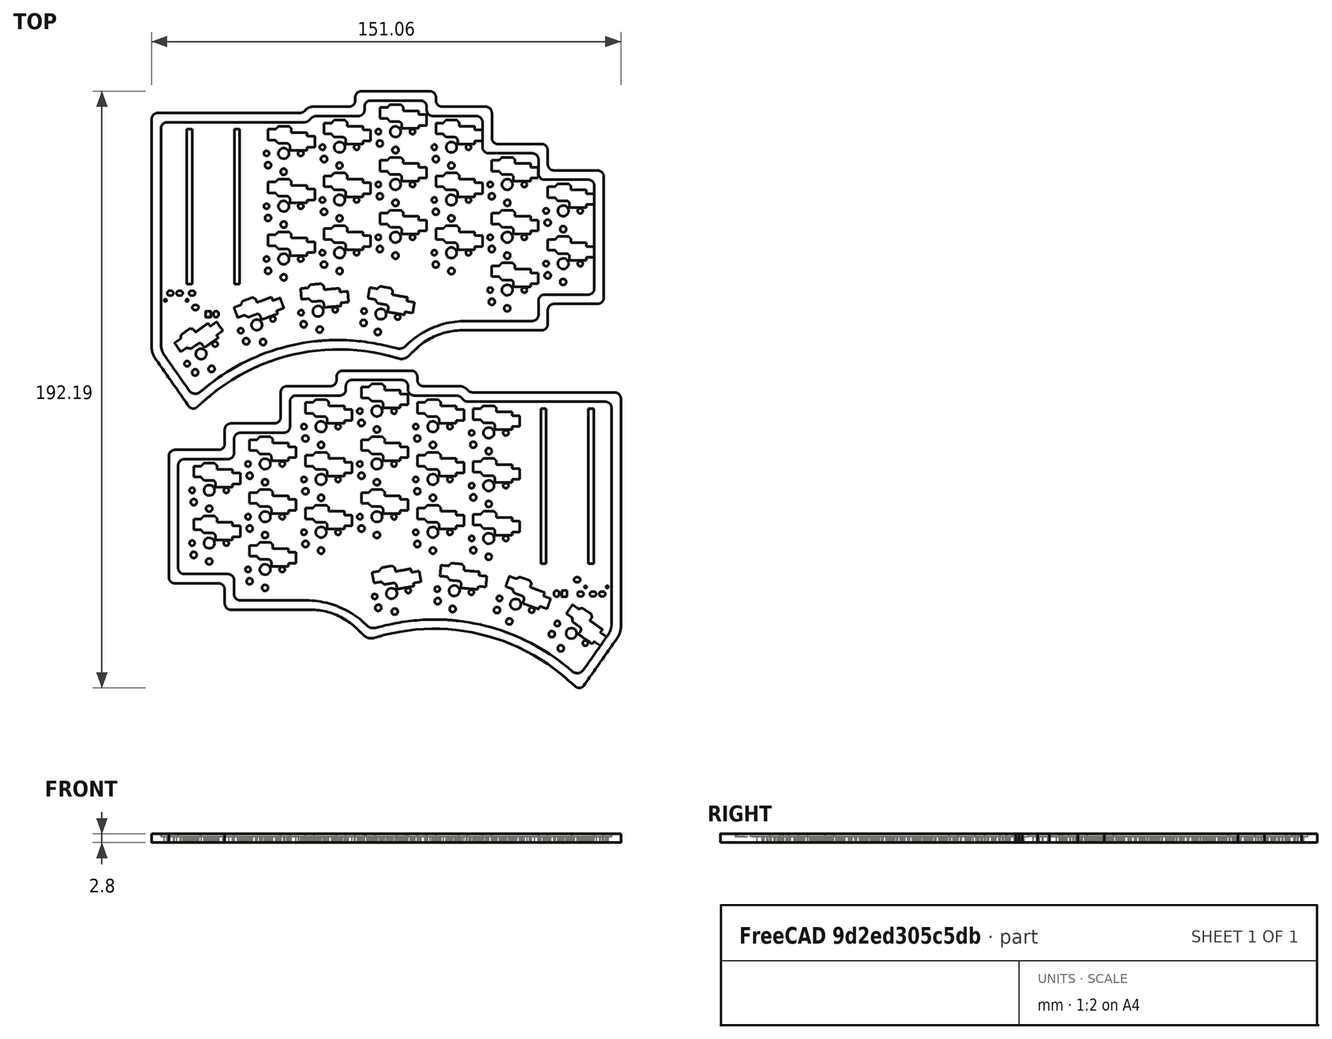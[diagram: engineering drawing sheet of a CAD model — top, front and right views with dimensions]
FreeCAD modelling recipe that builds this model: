
FCSTD DOCUMENT  (FreeCAD 0.21R33771 (Git))
Label: case_test
License: All rights reserved
LicenseURL: http://en.wikipedia.org/wiki/All_rights_reserved
objects: Part::Feature×276, Part::Extrusion×276, Part::MultiFuse×3, Part::FeaturePython×2, Part::Mirroring×1
note: 558 computed .brp shape members not serialized (recipe doc carries the construction recipe); baked Part::Feature solids carry a one-line shape summary decoded from their .brp

FEATURE [Part::Feature] path44149_5_3
  shape: bbox 145.5 x 102.4 x 2e-07 mm, 0 faces, 0 solids (baked)
FEATURE [Part::Extrusion] Extrude  label="bounds_left"
  Base = -> path44149_5_3
  Dir = (0,0,1)
  DirMode = 0
  FaceMakerClass = Part::FaceMakerBullseye
  LengthFwd = 2.8
  LengthRev = 0
  Placement = pos=(0,0,1) rot=(0,0,1;0rad)
  Solid = true
  Symmetric = false
FEATURE [Part::Feature] path44149_5_1
  shape: bbox 139.5 x 94.73 x 2e-07 mm, 0 faces, 0 solids (baked)
FEATURE [Part::Extrusion] Extrude001  label="inner_left"
  Base = -> path44149_5_1
  Dir = (0,0,1)
  DirMode = 0
  FaceMakerClass = Part::FaceMakerBullseye
  LengthFwd = 0.8
  LengthRev = 0
  Placement = pos=(0,0,3) rot=(0,0,1;0rad)
  Solid = true
  Symmetric = false
FEATURE [Part::Feature] path61609_4_5_7_9_4_80_0_5
  shape: bbox 15 x 7.701 x 2e-07 mm, 0 faces, 0 solids (baked)
FEATURE [Part::Feature] path61609_4_5_7_9_4_80_0_3_2
  shape: bbox 15 x 7.701 x 2e-07 mm, 0 faces, 0 solids (baked)
FEATURE [Part::Feature] path52377_09_3_1_8_87
  Placement = pos=(40.6315,-49.1329,0) rot=(0,0,1;0rad)
  shape: bbox 1.877 x 2.052 x 2e-07 mm, 0 faces, 0 solids (baked)
FEATURE [Part::Feature] path52401_71_2_4_9_8
  Placement = pos=(41.1315,-52.9329,0) rot=(0,0,1;0rad)
  shape: bbox 2.208 x 2.415 x 2e-07 mm, 0 faces, 0 solids (baked)
FEATURE [Part::Feature] path52401_7_8_1_8_2_30
  Placement = pos=(46.1315,-55.0329,0) rot=(0,0,1;0rad)
  shape: bbox 2.208 x 2.415 x 2e-07 mm, 0 faces, 0 solids (baked)
FEATURE [Part::Feature] path52377_0_5_0_4_2_3
  Placement = pos=(51.6315,-49.1329,0) rot=(0,0,1;0rad)
  shape: bbox 1.877 x 2.052 x 2e-07 mm, 0 faces, 0 solids (baked)
FEATURE [Part::Feature] path52456_0_5_5_7_86
  Placement = pos=(46.1315,-49.1329,0) rot=(0,0,1;0rad)
  shape: bbox 3.787 x 4.141 x 2e-07 mm, 0 faces, 0 solids (baked)
FEATURE [Part::Feature] path52377_09_3_1_8_8_2
  Placement = pos=(40.6315,-49.1329,0) rot=(0,0,1;0rad)
  shape: bbox 1.877 x 2.052 x 2e-07 mm, 0 faces, 0 solids (baked)
FEATURE [Part::Feature] path52401_71_2_4_9_4_5
  Placement = pos=(41.1315,-52.9329,0) rot=(0,0,1;0rad)
  shape: bbox 2.208 x 2.415 x 2e-07 mm, 0 faces, 0 solids (baked)
FEATURE [Part::Feature] path52401_7_8_1_8_2_3_11
  Placement = pos=(46.1315,-55.0329,0) rot=(0,0,1;0rad)
  shape: bbox 2.208 x 2.415 x 2e-07 mm, 0 faces, 0 solids (baked)
FEATURE [Part::Feature] path52377_0_5_0_4_2_4_5
  Placement = pos=(51.6315,-49.1329,0) rot=(0,0,1;0rad)
  shape: bbox 1.877 x 2.052 x 2e-07 mm, 0 faces, 0 solids (baked)
FEATURE [Part::Feature] path52456_0_5_5_7_7_0
  Placement = pos=(46.1315,-49.1329,0) rot=(0,0,1;0rad)
  shape: bbox 3.787 x 4.141 x 2e-07 mm, 0 faces, 0 solids (baked)
FEATURE [Part::Feature] path52377_09_3_1_8_2_3
  Placement = pos=(40.6315,-49.1329,0) rot=(0,0,1;0rad)
  shape: bbox 1.877 x 2.052 x 2e-07 mm, 0 faces, 0 solids (baked)
FEATURE [Part::Feature] path52401_71_2_4_9_2_39
  Placement = pos=(41.1315,-52.9329,0) rot=(0,0,1;0rad)
  shape: bbox 2.208 x 2.415 x 2e-07 mm, 0 faces, 0 solids (baked)
FEATURE [Part::Feature] path52401_7_8_1_8_2_31_2
  Placement = pos=(46.1315,-55.0329,0) rot=(0,0,1;0rad)
  shape: bbox 2.208 x 2.415 x 2e-07 mm, 0 faces, 0 solids (baked)
FEATURE [Part::Feature] path52377_0_5_0_4_2_41_1
  Placement = pos=(51.6315,-49.1329,0) rot=(0,0,1;0rad)
  shape: bbox 1.877 x 2.052 x 2e-07 mm, 0 faces, 0 solids (baked)
FEATURE [Part::Feature] path52456_0_5_5_7_4_2
  Placement = pos=(46.1315,-49.1329,0) rot=(0,0,1;0rad)
  shape: bbox 3.787 x 4.141 x 2e-07 mm, 0 faces, 0 solids (baked)
FEATURE [Part::Feature] path52377_09_3_1_8_2_4_7
  Placement = pos=(40.6315,-49.1329,0) rot=(0,0,1;0rad)
  shape: bbox 1.877 x 2.052 x 2e-07 mm, 0 faces, 0 solids (baked)
FEATURE [Part::Feature] path52401_71_2_4_9_2_9_8
  Placement = pos=(41.1315,-52.9329,0) rot=(0,0,1;0rad)
  shape: bbox 2.208 x 2.415 x 2e-07 mm, 0 faces, 0 solids (baked)
FEATURE [Part::Feature] path52401_7_8_1_8_2_31_5_4
  Placement = pos=(46.1315,-55.0329,0) rot=(0,0,1;0rad)
  shape: bbox 2.208 x 2.415 x 2e-07 mm, 0 faces, 0 solids (baked)
FEATURE [Part::Feature] path52377_0_5_0_4_2_41_0_0
  Placement = pos=(51.6315,-49.1329,0) rot=(0,0,1;0rad)
  shape: bbox 1.877 x 2.052 x 2e-07 mm, 0 faces, 0 solids (baked)
FEATURE [Part::Feature] path52456_0_5_5_7_4_4_1
  Placement = pos=(46.1315,-49.1329,0) rot=(0,0,1;0rad)
  shape: bbox 3.787 x 4.141 x 2e-07 mm, 0 faces, 0 solids (baked)
FEATURE [Part::Feature] path52377_09_3_1_8_8_0_3
  Placement = pos=(40.6315,-49.1329,0) rot=(0,0,1;0rad)
  shape: bbox 1.877 x 2.052 x 2e-07 mm, 0 faces, 0 solids (baked)
FEATURE [Part::Feature] path52401_71_2_4_9_4_2_0
  Placement = pos=(41.1315,-52.9329,0) rot=(0,0,1;0rad)
  shape: bbox 2.208 x 2.415 x 2e-07 mm, 0 faces, 0 solids (baked)
FEATURE [Part::Feature] path52401_7_8_1_8_2_3_5_0
  Placement = pos=(46.1315,-55.0329,0) rot=(0,0,1;0rad)
  shape: bbox 2.208 x 2.415 x 2e-07 mm, 0 faces, 0 solids (baked)
FEATURE [Part::Feature] path52377_0_5_0_4_2_4_4_3
  Placement = pos=(51.6315,-49.1329,0) rot=(0,0,1;0rad)
  shape: bbox 1.877 x 2.052 x 2e-07 mm, 0 faces, 0 solids (baked)
FEATURE [Part::Feature] path52456_0_5_5_7_7_7_7
  Placement = pos=(46.1315,-49.1329,0) rot=(0,0,1;0rad)
  shape: bbox 3.787 x 4.141 x 2e-07 mm, 0 faces, 0 solids (baked)
FEATURE [Part::Feature] path52377_09_3_1_8_2_9_7
  Placement = pos=(40.6315,-49.1329,0) rot=(0,0,1;0rad)
  shape: bbox 1.877 x 2.052 x 2e-07 mm, 0 faces, 0 solids (baked)
FEATURE [Part::Feature] path52401_71_2_4_9_2_6_0
  Placement = pos=(41.1315,-52.9329,0) rot=(0,0,1;0rad)
  shape: bbox 2.208 x 2.415 x 2e-07 mm, 0 faces, 0 solids (baked)
FEATURE [Part::Feature] path52401_7_8_1_8_2_31_56_74
  Placement = pos=(46.1315,-55.0329,0) rot=(0,0,1;0rad)
  shape: bbox 2.208 x 2.415 x 2e-07 mm, 0 faces, 0 solids (baked)
FEATURE [Part::Feature] path52377_0_5_0_4_2_41_4_91
  Placement = pos=(51.6315,-49.1329,0) rot=(0,0,1;0rad)
  shape: bbox 1.877 x 2.052 x 2e-07 mm, 0 faces, 0 solids (baked)
FEATURE [Part::Feature] path52456_0_5_5_7_4_40_0
  Placement = pos=(46.1315,-49.1329,0) rot=(0,0,1;0rad)
  shape: bbox 3.787 x 4.141 x 2e-07 mm, 0 faces, 0 solids (baked)
FEATURE [Part::Feature] path52377_09_3_1_8_2_4_0_1
  Placement = pos=(40.6315,-49.1329,0) rot=(0,0,1;0rad)
  shape: bbox 1.877 x 2.052 x 2e-07 mm, 0 faces, 0 solids (baked)
FEATURE [Part::Feature] path52401_71_2_4_9_2_9_9_55
  Placement = pos=(41.1315,-52.9329,0) rot=(0,0,1;0rad)
  shape: bbox 2.208 x 2.415 x 2e-07 mm, 0 faces, 0 solids (baked)
FEATURE [Part::Feature] path52401_7_8_1_8_2_31_5_9_4
  Placement = pos=(46.1315,-55.0329,0) rot=(0,0,1;0rad)
  shape: bbox 2.208 x 2.415 x 2e-07 mm, 0 faces, 0 solids (baked)
FEATURE [Part::Feature] path52377_0_5_0_4_2_41_0_4_8
  Placement = pos=(51.6315,-49.1329,0) rot=(0,0,1;0rad)
  shape: bbox 1.877 x 2.052 x 2e-07 mm, 0 faces, 0 solids (baked)
FEATURE [Part::Feature] path52456_0_5_5_7_4_4_8_02
  Placement = pos=(46.1315,-49.1329,0) rot=(0,0,1;0rad)
  shape: bbox 3.787 x 4.141 x 2e-07 mm, 0 faces, 0 solids (baked)
FEATURE [Part::Feature] path52377_09_3_1_8_8_0_4_7
  Placement = pos=(40.6315,-49.1329,0) rot=(0,0,1;0rad)
  shape: bbox 1.877 x 2.052 x 2e-07 mm, 0 faces, 0 solids (baked)
FEATURE [Part::Feature] path52401_71_2_4_9_4_2_2_1
  Placement = pos=(41.1315,-52.9329,0) rot=(0,0,1;0rad)
  shape: bbox 2.208 x 2.415 x 2e-07 mm, 0 faces, 0 solids (baked)
FEATURE [Part::Feature] path52401_7_8_1_8_2_3_5_3_8
  Placement = pos=(46.1315,-55.0329,0) rot=(0,0,1;0rad)
  shape: bbox 2.208 x 2.415 x 2e-07 mm, 0 faces, 0 solids (baked)
FEATURE [Part::Feature] path52377_0_5_0_4_2_4_4_8_3
  Placement = pos=(51.6315,-49.1329,0) rot=(0,0,1;0rad)
  shape: bbox 1.877 x 2.052 x 2e-07 mm, 0 faces, 0 solids (baked)
FEATURE [Part::Feature] path52456_0_5_5_7_7_7_1_3
  Placement = pos=(46.1315,-49.1329,0) rot=(0,0,1;0rad)
  shape: bbox 3.787 x 4.141 x 2e-07 mm, 0 faces, 0 solids (baked)
FEATURE [Part::Feature] path52377_09_3_1_8_2_9_5_3
  Placement = pos=(40.6315,-49.1329,0) rot=(0,0,1;0rad)
  shape: bbox 1.877 x 2.052 x 2e-07 mm, 0 faces, 0 solids (baked)
FEATURE [Part::Feature] path52401_71_2_4_9_2_6_3_64
  Placement = pos=(41.1315,-52.9329,0) rot=(0,0,1;0rad)
  shape: bbox 2.208 x 2.415 x 2e-07 mm, 0 faces, 0 solids (baked)
FEATURE [Part::Feature] path52401_7_8_1_8_2_31_56_1_9
  Placement = pos=(46.1315,-55.0329,0) rot=(0,0,1;0rad)
  shape: bbox 2.208 x 2.415 x 2e-07 mm, 0 faces, 0 solids (baked)
FEATURE [Part::Feature] path52377_0_5_0_4_2_41_4_8_1
  Placement = pos=(51.6315,-49.1329,0) rot=(0,0,1;0rad)
  shape: bbox 1.877 x 2.052 x 2e-07 mm, 0 faces, 0 solids (baked)
FEATURE [Part::Feature] path52456_0_5_5_7_4_40_5_0
  Placement = pos=(46.1315,-49.1329,0) rot=(0,0,1;0rad)
  shape: bbox 3.787 x 4.141 x 2e-07 mm, 0 faces, 0 solids (baked)
FEATURE [Part::Feature] path52377_09_3_1_8_2_4_0_5_8
  Placement = pos=(40.6315,-49.1329,0) rot=(0,0,1;0rad)
  shape: bbox 1.877 x 2.052 x 2e-07 mm, 0 faces, 0 solids (baked)
FEATURE [Part::Feature] path52401_71_2_4_9_2_9_9_5_64
  Placement = pos=(41.1315,-52.9329,0) rot=(0,0,1;0rad)
  shape: bbox 2.208 x 2.415 x 2e-07 mm, 0 faces, 0 solids (baked)
FEATURE [Part::Feature] path52401_7_8_1_8_2_31_5_9_9_9
  Placement = pos=(46.1315,-55.0329,0) rot=(0,0,1;0rad)
  shape: bbox 2.208 x 2.415 x 2e-07 mm, 0 faces, 0 solids (baked)
FEATURE [Part::Feature] path52377_0_5_0_4_2_41_0_4_1_4
  Placement = pos=(51.6315,-49.1329,0) rot=(0,0,1;0rad)
  shape: bbox 1.877 x 2.052 x 2e-07 mm, 0 faces, 0 solids (baked)
FEATURE [Part::Feature] path52456_0_5_5_7_4_4_8_5_4
  Placement = pos=(46.1315,-49.1329,0) rot=(0,0,1;0rad)
  shape: bbox 3.787 x 4.141 x 2e-07 mm, 0 faces, 0 solids (baked)
FEATURE [Part::Feature] path52377_09_3_1_8_8_0_4_5_6
  Placement = pos=(40.6315,-49.1329,0) rot=(0,0,1;0rad)
  shape: bbox 1.877 x 2.052 x 2e-07 mm, 0 faces, 0 solids (baked)
FEATURE [Part::Feature] path52401_71_2_4_9_4_2_2_8_5
  Placement = pos=(41.1315,-52.9329,0) rot=(0,0,1;0rad)
  shape: bbox 2.208 x 2.415 x 2e-07 mm, 0 faces, 0 solids (baked)
FEATURE [Part::Feature] path52401_7_8_1_8_2_3_5_3_4_2
  Placement = pos=(46.1315,-55.0329,0) rot=(0,0,1;0rad)
  shape: bbox 2.208 x 2.415 x 2e-07 mm, 0 faces, 0 solids (baked)
FEATURE [Part::Feature] path52377_0_5_0_4_2_4_4_8_9_1
  Placement = pos=(51.6315,-49.1329,0) rot=(0,0,1;0rad)
  shape: bbox 1.877 x 2.052 x 2e-07 mm, 0 faces, 0 solids (baked)
FEATURE [Part::Feature] path52456_0_5_5_7_7_7_1_7_8
  Placement = pos=(46.1315,-49.1329,0) rot=(0,0,1;0rad)
  shape: bbox 3.787 x 4.141 x 2e-07 mm, 0 faces, 0 solids (baked)
FEATURE [Part::Feature] path52377_09_3_1_8_2_9_5_4_8
  Placement = pos=(40.6315,-49.1329,0) rot=(0,0,1;0rad)
  shape: bbox 1.877 x 2.052 x 2e-07 mm, 0 faces, 0 solids (baked)
FEATURE [Part::Feature] path52401_71_2_4_9_2_6_3_6_9
  Placement = pos=(41.1315,-52.9329,0) rot=(0,0,1;0rad)
  shape: bbox 2.208 x 2.415 x 2e-07 mm, 0 faces, 0 solids (baked)
FEATURE [Part::Feature] path52401_7_8_1_8_2_31_56_1_3_7
  Placement = pos=(46.1315,-55.0329,0) rot=(0,0,1;0rad)
  shape: bbox 2.208 x 2.415 x 2e-07 mm, 0 faces, 0 solids (baked)
FEATURE [Part::Feature] path52377_0_5_0_4_2_41_4_8_8_6
  Placement = pos=(51.6315,-49.1329,0) rot=(0,0,1;0rad)
  shape: bbox 1.877 x 2.052 x 2e-07 mm, 0 faces, 0 solids (baked)
FEATURE [Part::Feature] path52456_0_5_5_7_4_40_5_1_45
  Placement = pos=(46.1315,-49.1329,0) rot=(0,0,1;0rad)
  shape: bbox 3.787 x 4.141 x 2e-07 mm, 0 faces, 0 solids (baked)
FEATURE [Part::Feature] path52377_09_3_1_8_2_4_0_5_0_4
  Placement = pos=(40.6315,-49.1329,0) rot=(0,0,1;0rad)
  shape: bbox 1.877 x 2.052 x 2e-07 mm, 0 faces, 0 solids (baked)
FEATURE [Part::Feature] path52401_71_2_4_9_2_9_9_5_6_8
  Placement = pos=(41.1315,-52.9329,0) rot=(0,0,1;0rad)
  shape: bbox 2.208 x 2.415 x 2e-07 mm, 0 faces, 0 solids (baked)
FEATURE [Part::Feature] path52401_7_8_1_8_2_31_5_9_9_0_0
  Placement = pos=(46.1315,-55.0329,0) rot=(0,0,1;0rad)
  shape: bbox 2.208 x 2.415 x 2e-07 mm, 0 faces, 0 solids (baked)
FEATURE [Part::Feature] path52377_0_5_0_4_2_41_0_4_1_8_44
  Placement = pos=(51.6315,-49.1329,0) rot=(0,0,1;0rad)
  shape: bbox 1.877 x 2.052 x 2e-07 mm, 0 faces, 0 solids (baked)
FEATURE [Part::Feature] path52456_0_5_5_7_4_4_8_5_8_8
  Placement = pos=(46.1315,-49.1329,0) rot=(0,0,1;0rad)
  shape: bbox 3.787 x 4.141 x 2e-07 mm, 0 faces, 0 solids (baked)
FEATURE [Part::Feature] path52377_09_3_1_8_8_0_4_5_8_91
  Placement = pos=(40.6315,-49.1329,0) rot=(0,0,1;0rad)
  shape: bbox 1.877 x 2.052 x 2e-07 mm, 0 faces, 0 solids (baked)
FEATURE [Part::Feature] path52401_71_2_4_9_4_2_2_8_7_5
  Placement = pos=(41.1315,-52.9329,0) rot=(0,0,1;0rad)
  shape: bbox 2.208 x 2.415 x 2e-07 mm, 0 faces, 0 solids (baked)
FEATURE [Part::Feature] path52401_7_8_1_8_2_3_5_3_4_4_44
  Placement = pos=(46.1315,-55.0329,0) rot=(0,0,1;0rad)
  shape: bbox 2.208 x 2.415 x 2e-07 mm, 0 faces, 0 solids (baked)
FEATURE [Part::Feature] path52377_0_5_0_4_2_4_4_8_9_2_9
  Placement = pos=(51.6315,-49.1329,0) rot=(0,0,1;0rad)
  shape: bbox 1.877 x 2.052 x 2e-07 mm, 0 faces, 0 solids (baked)
FEATURE [Part::Feature] path52456_0_5_5_7_7_7_1_7_0_2
  Placement = pos=(46.1315,-49.1329,0) rot=(0,0,1;0rad)
  shape: bbox 3.787 x 4.141 x 2e-07 mm, 0 faces, 0 solids (baked)
FEATURE [Part::Feature] path52377_09_3_1_8_2_9_5_4_9_5
  Placement = pos=(40.6315,-49.1329,0) rot=(0,0,1;0rad)
  shape: bbox 1.877 x 2.052 x 2e-07 mm, 0 faces, 0 solids (baked)
FEATURE [Part::Feature] path52401_71_2_4_9_2_6_3_6_8_5
  Placement = pos=(41.1315,-52.9329,0) rot=(0,0,1;0rad)
  shape: bbox 2.208 x 2.415 x 2e-07 mm, 0 faces, 0 solids (baked)
FEATURE [Part::Feature] path52401_7_8_1_8_2_31_56_1_3_0_2
  Placement = pos=(46.1315,-55.0329,0) rot=(0,0,1;0rad)
  shape: bbox 2.208 x 2.415 x 2e-07 mm, 0 faces, 0 solids (baked)
FEATURE [Part::Feature] path52377_0_5_0_4_2_41_4_8_8_0_5
  Placement = pos=(51.6315,-49.1329,0) rot=(0,0,1;0rad)
  shape: bbox 1.877 x 2.052 x 2e-07 mm, 0 faces, 0 solids (baked)
FEATURE [Part::Feature] path52456_0_5_5_7_4_40_5_1_5_56
  Placement = pos=(46.1315,-49.1329,0) rot=(0,0,1;0rad)
  shape: bbox 3.787 x 4.141 x 2e-07 mm, 0 faces, 0 solids (baked)
FEATURE [Part::Feature] path52377_09_3_1_8_2_4_0_5_0_2_7
  Placement = pos=(40.6315,-49.1329,0) rot=(0,0,1;0rad)
  shape: bbox 1.877 x 2.052 x 2e-07 mm, 0 faces, 0 solids (baked)
FEATURE [Part::Feature] path52401_71_2_4_9_2_9_9_5_6_2_6
  Placement = pos=(41.1315,-52.9329,0) rot=(0,0,1;0rad)
  shape: bbox 2.208 x 2.415 x 2e-07 mm, 0 faces, 0 solids (baked)
FEATURE [Part::Feature] path52401_7_8_1_8_2_31_5_9_9_0_7_2
  Placement = pos=(46.1315,-55.0329,0) rot=(0,0,1;0rad)
  shape: bbox 2.208 x 2.415 x 2e-07 mm, 0 faces, 0 solids (baked)
FEATURE [Part::Feature] path52377_0_5_0_4_2_41_0_4_1_8_4_4
  Placement = pos=(51.6315,-49.1329,0) rot=(0,0,1;0rad)
  shape: bbox 1.877 x 2.052 x 2e-07 mm, 0 faces, 0 solids (baked)
FEATURE [Part::Feature] path52456_0_5_5_7_4_4_8_5_8_0_3
  Placement = pos=(46.1315,-49.1329,0) rot=(0,0,1;0rad)
  shape: bbox 3.787 x 4.141 x 2e-07 mm, 0 faces, 0 solids (baked)
FEATURE [Part::Feature] path52377_09_3_1_8_8_0_4_5_8_9_1
  Placement = pos=(40.6315,-49.1329,0) rot=(0,0,1;0rad)
  shape: bbox 1.877 x 2.052 x 2e-07 mm, 0 faces, 0 solids (baked)
FEATURE [Part::Feature] path52401_71_2_4_9_4_2_2_8_7_6_2
  Placement = pos=(41.1315,-52.9329,0) rot=(0,0,1;0rad)
  shape: bbox 2.208 x 2.415 x 2e-07 mm, 0 faces, 0 solids (baked)
FEATURE [Part::Feature] path52401_7_8_1_8_2_3_5_3_4_4_8_8
  Placement = pos=(46.1315,-55.0329,0) rot=(0,0,1;0rad)
  shape: bbox 2.208 x 2.415 x 2e-07 mm, 0 faces, 0 solids (baked)
FEATURE [Part::Feature] path52377_0_5_0_4_2_4_4_8_9_2_0_5
  Placement = pos=(51.6315,-49.1329,0) rot=(0,0,1;0rad)
  shape: bbox 1.877 x 2.052 x 2e-07 mm, 0 faces, 0 solids (baked)
FEATURE [Part::Feature] path52456_0_5_5_7_7_7_1_7_0_0_6
  Placement = pos=(46.1315,-49.1329,0) rot=(0,0,1;0rad)
  shape: bbox 3.787 x 4.141 x 2e-07 mm, 0 faces, 0 solids (baked)
FEATURE [Part::Feature] circle37307_9_0_7_1
  Placement = pos=(138.24,-66.7421,0) rot=(0,0,1;0rad)
  shape: bbox 0.8832 x 0.9658 x 2e-07 mm, 0 faces, 0 solids (baked)
FEATURE [Part::Feature] circle37313_0_5_2_6
  Placement = pos=(131.24,-66.7421,0) rot=(0,0,1;0rad)
  shape: bbox 0.8832 x 0.9658 x 2e-07 mm, 0 faces, 0 solids (baked)
FEATURE [Part::Feature] path8_2
  shape: bbox 2.002 x 1.601 x 2e-07 mm, 0 faces, 0 solids (baked)
FEATURE [Part::Feature] path4_1
  shape: bbox 2.002 x 1.601 x 2e-07 mm, 0 faces, 0 solids (baked)
FEATURE [Part::Feature] path6_5
  shape: bbox 2.002 x 1.601 x 2e-07 mm, 0 faces, 0 solids (baked)
FEATURE [Part::Feature] path2_5
  shape: bbox 2.002 x 1.601 x 2e-07 mm, 0 faces, 0 solids (baked)
FEATURE [Part::Feature] path37931_6_3_3
  shape: bbox 1.7 x 2 x 2e-07 mm, 0 faces, 0 solids (baked)
FEATURE [Part::Feature] path37937_8_1_8
  shape: bbox 1.702 x 2 x 2e-07 mm, 0 faces, 0 solids (baked)
FEATURE [Part::Feature] rect117948_1_5_1_8
  shape: bbox 1.7 x 49.96 x 2e-07 mm, 0 faces, 0 solids (baked)
FEATURE [Part::Feature] rect117948_2_0_8_5_8
  shape: bbox 1.7 x 49.96 x 2e-07 mm, 0 faces, 0 solids (baked)
FEATURE [Part::Feature] path61609_4_5_7_9_4_80_0_8_78
  shape: bbox 15 x 7.701 x 2e-07 mm, 0 faces, 0 solids (baked)
FEATURE [Part::Feature] path61609_4_5_7_9_4_80_0_3_8_68
  shape: bbox 15 x 7.701 x 2e-07 mm, 0 faces, 0 solids (baked)
FEATURE [Part::Feature] path61609_4_5_7_9_4_80_0_3_8_6_79
  shape: bbox 15 x 7.701 x 2e-07 mm, 0 faces, 0 solids (baked)
FEATURE [Part::Feature] path61609_4_5_7_9_4_80_0_8_3_5
  shape: bbox 15 x 7.701 x 2e-07 mm, 0 faces, 0 solids (baked)
FEATURE [Part::Feature] path61609_4_5_7_9_4_80_0_3_8_9_3
  shape: bbox 15 x 7.701 x 2e-07 mm, 0 faces, 0 solids (baked)
FEATURE [Part::Feature] path61609_4_5_7_9_4_80_0_3_8_6_1_2
  shape: bbox 15 x 7.701 x 2e-07 mm, 0 faces, 0 solids (baked)
FEATURE [Part::Feature] path61609_4_5_7_9_4_80_0_8_7_0
  shape: bbox 15 x 7.701 x 2e-07 mm, 0 faces, 0 solids (baked)
FEATURE [Part::Feature] path61609_4_5_7_9_4_80_0_3_8_91_1
  shape: bbox 15 x 7.701 x 2e-07 mm, 0 faces, 0 solids (baked)
FEATURE [Part::Feature] path61609_4_5_7_9_4_80_0_3_8_6_3_6
  shape: bbox 15 x 7.701 x 2e-07 mm, 0 faces, 0 solids (baked)
FEATURE [Part::Feature] path61609_4_5_7_9_4_80_0_8_8_6
  shape: bbox 15 x 7.701 x 2e-07 mm, 0 faces, 0 solids (baked)
FEATURE [Part::Feature] path61609_4_5_7_9_4_80_0_3_8_0_9
  shape: bbox 15 x 7.701 x 2e-07 mm, 0 faces, 0 solids (baked)
FEATURE [Part::Feature] path61609_4_5_7_9_4_80_0_3_8_6_7_8
  shape: bbox 15 x 7.701 x 2e-07 mm, 0 faces, 0 solids (baked)
FEATURE [Part::Feature] path61609_4_5_7_9_4_80_0_8_2_6
  shape: bbox 15 x 7.701 x 2e-07 mm, 0 faces, 0 solids (baked)
FEATURE [Part::Feature] path61609_4_5_7_9_4_80_0_3_8_60_6
  shape: bbox 15 x 7.701 x 2e-07 mm, 0 faces, 0 solids (baked)
FEATURE [Part::Feature] path61609_4_5_7_9_4_80_0_3_8_6_4_2
  shape: bbox 15 x 7.701 x 2e-07 mm, 0 faces, 0 solids (baked)
FEATURE [Part::Feature] path52377_09_3_5_7_6_7_3_2
  Placement = pos=(40.6315,-49.1329,0) rot=(0,0,1;0rad)
  shape: bbox 2.046 x 1.998 x 2e-07 mm, 0 faces, 0 solids (baked)
FEATURE [Part::Feature] path52401_71_2_5_9_2_77_3_4
  Placement = pos=(41.1315,-52.9329,0) rot=(0,0,1;0rad)
  shape: bbox 2.407 x 2.351 x 2e-07 mm, 0 faces, 0 solids (baked)
FEATURE [Part::Feature] path52401_7_8_1_1_7_3_9_0_7
  Placement = pos=(46.1315,-55.0329,0) rot=(0,0,1;0rad)
  shape: bbox 2.407 x 2.351 x 2e-07 mm, 0 faces, 0 solids (baked)
FEATURE [Part::Feature] path52377_0_5_0_1_9_1_5_5_6
  Placement = pos=(51.6315,-49.1329,0) rot=(0,0,1;0rad)
  shape: bbox 2.046 x 1.998 x 2e-07 mm, 0 faces, 0 solids (baked)
FEATURE [Part::Feature] path52456_0_5_2_2_2_3_5_8
  Placement = pos=(46.1315,-49.1329,0) rot=(0,0,1;0rad)
  shape: bbox 4.128 x 4.032 x 2e-07 mm, 0 faces, 0 solids (baked)
FEATURE [Part::Feature] path52377_09_3_5_7_6_0_0_2_2
  Placement = pos=(40.6315,-49.1329,0) rot=(0,0,1;0rad)
  shape: bbox 2.028 x 2.027 x 2e-07 mm, 0 faces, 0 solids (baked)
FEATURE [Part::Feature] path52401_71_2_5_9_2_7_5_4_9
  Placement = pos=(41.1315,-52.9329,0) rot=(0,0,1;0rad)
  shape: bbox 2.386 x 2.384 x 2e-07 mm, 0 faces, 0 solids (baked)
FEATURE [Part::Feature] path52401_7_8_1_1_7_3_8_4_4_6
  Placement = pos=(46.1315,-55.0329,0) rot=(0,0,1;0rad)
  shape: bbox 2.386 x 2.384 x 2e-07 mm, 0 faces, 0 solids (baked)
FEATURE [Part::Feature] path52377_0_5_0_1_9_1_0_6_9_1
  Placement = pos=(51.6315,-49.1329,0) rot=(0,0,1;0rad)
  shape: bbox 2.028 x 2.027 x 2e-07 mm, 0 faces, 0 solids (baked)
FEATURE [Part::Feature] path52456_0_5_2_2_2_9_9_3_1
  Placement = pos=(46.1315,-49.1329,0) rot=(0,0,1;0rad)
  shape: bbox 4.091 x 4.089 x 2e-07 mm, 0 faces, 0 solids (baked)
FEATURE [Part::Feature] path52377_09_3_5_7_6_6_7_9_0
  Placement = pos=(40.6315,-49.1329,0) rot=(0,0,1;0rad)
  shape: bbox 2 x 2.046 x 2e-07 mm, 0 faces, 0 solids (baked)
FEATURE [Part::Feature] path52401_71_2_5_9_2_1_4_5_2
  Placement = pos=(41.1315,-52.9329,0) rot=(0,0,1;0rad)
  shape: bbox 2.353 x 2.407 x 2e-07 mm, 0 faces, 0 solids (baked)
FEATURE [Part::Feature] path52401_7_8_1_1_7_3_1_9_1_9
  Placement = pos=(46.1315,-55.0329,0) rot=(0,0,1;0rad)
  shape: bbox 2.353 x 2.407 x 2e-07 mm, 0 faces, 0 solids (baked)
FEATURE [Part::Feature] path52377_0_5_0_1_9_1_3_9_3_6
  Placement = pos=(51.6315,-49.1329,0) rot=(0,0,1;0rad)
  shape: bbox 2 x 2.046 x 2e-07 mm, 0 faces, 0 solids (baked)
FEATURE [Part::Feature] path52456_0_5_2_2_2_5_8_5_5
  Placement = pos=(46.1315,-49.1329,0) rot=(0,0,1;0rad)
  shape: bbox 4.036 x 4.128 x 2e-07 mm, 0 faces, 0 solids (baked)
FEATURE [Part::Feature] path52377_09_3_5_7_6_4_7_2_2
  Placement = pos=(40.6315,-49.1329,0) rot=(0,0,1;0rad)
  shape: bbox 2.027 x 2.028 x 2e-07 mm, 0 faces, 0 solids (baked)
FEATURE [Part::Feature] path52401_71_2_5_9_2_8_0_6_1
  Placement = pos=(41.1315,-52.9329,0) rot=(0,0,1;0rad)
  shape: bbox 2.385 x 2.386 x 2e-07 mm, 0 faces, 0 solids (baked)
FEATURE [Part::Feature] path52401_7_8_1_1_7_3_6_7_6_3
  Placement = pos=(46.1315,-55.0329,0) rot=(0,0,1;0rad)
  shape: bbox 2.385 x 2.386 x 2e-07 mm, 0 faces, 0 solids (baked)
FEATURE [Part::Feature] path52377_0_5_0_1_9_1_4_7_5_3
  Placement = pos=(51.6315,-49.1329,0) rot=(0,0,1;0rad)
  shape: bbox 2.027 x 2.028 x 2e-07 mm, 0 faces, 0 solids (baked)
FEATURE [Part::Feature] path52456_0_5_2_2_2_7_4_6_3
  Placement = pos=(46.1315,-49.1329,0) rot=(0,0,1;0rad)
  shape: bbox 4.09 x 4.092 x 2e-07 mm, 0 faces, 0 solids (baked)
FEATURE [Part::Feature] path61609_4_5_7_9_4_80_0_8_2_8_3_3
  shape: bbox 15.78 x 7.528 x 2e-07 mm, 0 faces, 0 solids (baked)
FEATURE [Part::Feature] path61609_4_5_7_9_4_80_0_8_2_8_3_6_9
  shape: bbox 15.05 x 8.449 x 2e-07 mm, 0 faces, 0 solids (baked)
FEATURE [Part::Feature] path61609_4_5_7_9_4_80_0_8_2_8_3_69_9
  shape: bbox 14.53 x 10.59 x 2e-07 mm, 0 faces, 0 solids (baked)
FEATURE [Part::Feature] path61609_4_5_7_9_4_80_0_8_2_8_3_7_7
  shape: bbox 13.03 x 13.29 x 2e-07 mm, 0 faces, 0 solids (baked)
FEATURE [Part::Extrusion] Extrude012
  Base = -> path61609_4_5_7_9_4_80_0_5
  Dir = (0,0,1)
  DirMode = 0
  FaceMakerClass = Part::FaceMakerBullseye
  LengthFwd = 2
  LengthRev = 0
  Solid = true
  Symmetric = false
FEATURE [Part::Extrusion] Extrude013
  Base = -> path61609_4_5_7_9_4_80_0_3_2
  Dir = (0,0,1)
  DirMode = 0
  FaceMakerClass = Part::FaceMakerBullseye
  LengthFwd = 2
  LengthRev = 0
  Solid = true
  Symmetric = false
FEATURE [Part::Extrusion] Extrude014
  Base = -> path52377_09_3_1_8_87
  Dir = (0,0,1)
  DirMode = 0
  FaceMakerClass = Part::FaceMakerBullseye
  LengthFwd = 2
  LengthRev = 0
  Solid = true
  Symmetric = false
FEATURE [Part::Extrusion] Extrude015
  Base = -> path52401_71_2_4_9_8
  Dir = (0,0,1)
  DirMode = 0
  FaceMakerClass = Part::FaceMakerBullseye
  LengthFwd = 2
  LengthRev = 0
  Solid = true
  Symmetric = false
FEATURE [Part::Extrusion] Extrude016
  Base = -> path52401_7_8_1_8_2_30
  Dir = (0,0,1)
  DirMode = 0
  FaceMakerClass = Part::FaceMakerBullseye
  LengthFwd = 2
  LengthRev = 0
  Solid = true
  Symmetric = false
FEATURE [Part::Extrusion] Extrude017
  Base = -> path52377_0_5_0_4_2_3
  Dir = (0,0,1)
  DirMode = 0
  FaceMakerClass = Part::FaceMakerBullseye
  LengthFwd = 2
  LengthRev = 0
  Solid = true
  Symmetric = false
FEATURE [Part::Extrusion] Extrude018
  Base = -> path52456_0_5_5_7_86
  Dir = (0,0,1)
  DirMode = 0
  FaceMakerClass = Part::FaceMakerBullseye
  LengthFwd = 2
  LengthRev = 0
  Solid = true
  Symmetric = false
FEATURE [Part::Extrusion] Extrude019
  Base = -> path52377_09_3_1_8_8_2
  Dir = (0,0,1)
  DirMode = 0
  FaceMakerClass = Part::FaceMakerBullseye
  LengthFwd = 2
  LengthRev = 0
  Solid = true
  Symmetric = false
FEATURE [Part::Extrusion] Extrude020
  Base = -> path52401_71_2_4_9_4_5
  Dir = (0,0,1)
  DirMode = 0
  FaceMakerClass = Part::FaceMakerBullseye
  LengthFwd = 2
  LengthRev = 0
  Solid = true
  Symmetric = false
FEATURE [Part::Extrusion] Extrude021
  Base = -> path52401_7_8_1_8_2_3_11
  Dir = (0,0,1)
  DirMode = 0
  FaceMakerClass = Part::FaceMakerBullseye
  LengthFwd = 2
  LengthRev = 0
  Solid = true
  Symmetric = false
FEATURE [Part::Extrusion] Extrude022
  Base = -> path52377_0_5_0_4_2_4_5
  Dir = (0,0,1)
  DirMode = 0
  FaceMakerClass = Part::FaceMakerBullseye
  LengthFwd = 2
  LengthRev = 0
  Solid = true
  Symmetric = false
FEATURE [Part::Extrusion] Extrude023
  Base = -> path52456_0_5_5_7_7_0
  Dir = (0,0,1)
  DirMode = 0
  FaceMakerClass = Part::FaceMakerBullseye
  LengthFwd = 2
  LengthRev = 0
  Solid = true
  Symmetric = false
FEATURE [Part::Extrusion] Extrude024
  Base = -> path52377_09_3_1_8_2_3
  Dir = (0,0,1)
  DirMode = 0
  FaceMakerClass = Part::FaceMakerBullseye
  LengthFwd = 2
  LengthRev = 0
  Solid = true
  Symmetric = false
FEATURE [Part::Extrusion] Extrude025
  Base = -> path52401_71_2_4_9_2_39
  Dir = (0,0,1)
  DirMode = 0
  FaceMakerClass = Part::FaceMakerBullseye
  LengthFwd = 2
  LengthRev = 0
  Solid = true
  Symmetric = false
FEATURE [Part::Extrusion] Extrude026
  Base = -> path52401_7_8_1_8_2_31_2
  Dir = (0,0,1)
  DirMode = 0
  FaceMakerClass = Part::FaceMakerBullseye
  LengthFwd = 2
  LengthRev = 0
  Solid = true
  Symmetric = false
FEATURE [Part::Extrusion] Extrude027
  Base = -> path52377_0_5_0_4_2_41_1
  Dir = (0,0,1)
  DirMode = 0
  FaceMakerClass = Part::FaceMakerBullseye
  LengthFwd = 2
  LengthRev = 0
  Solid = true
  Symmetric = false
FEATURE [Part::Extrusion] Extrude028
  Base = -> path52456_0_5_5_7_4_2
  Dir = (0,0,1)
  DirMode = 0
  FaceMakerClass = Part::FaceMakerBullseye
  LengthFwd = 2
  LengthRev = 0
  Solid = true
  Symmetric = false
FEATURE [Part::Extrusion] Extrude029
  Base = -> path52377_09_3_1_8_2_4_7
  Dir = (0,0,1)
  DirMode = 0
  FaceMakerClass = Part::FaceMakerBullseye
  LengthFwd = 2
  LengthRev = 0
  Solid = true
  Symmetric = false
FEATURE [Part::Extrusion] Extrude030
  Base = -> path52401_71_2_4_9_2_9_8
  Dir = (0,0,1)
  DirMode = 0
  FaceMakerClass = Part::FaceMakerBullseye
  LengthFwd = 2
  LengthRev = 0
  Solid = true
  Symmetric = false
FEATURE [Part::Extrusion] Extrude031
  Base = -> path52401_7_8_1_8_2_31_5_4
  Dir = (0,0,1)
  DirMode = 0
  FaceMakerClass = Part::FaceMakerBullseye
  LengthFwd = 2
  LengthRev = 0
  Solid = true
  Symmetric = false
FEATURE [Part::Extrusion] Extrude032
  Base = -> path52377_0_5_0_4_2_41_0_0
  Dir = (0,0,1)
  DirMode = 0
  FaceMakerClass = Part::FaceMakerBullseye
  LengthFwd = 2
  LengthRev = 0
  Solid = true
  Symmetric = false
FEATURE [Part::Extrusion] Extrude033
  Base = -> path52456_0_5_5_7_4_4_1
  Dir = (0,0,1)
  DirMode = 0
  FaceMakerClass = Part::FaceMakerBullseye
  LengthFwd = 2
  LengthRev = 0
  Solid = true
  Symmetric = false
FEATURE [Part::Extrusion] Extrude034
  Base = -> path52377_09_3_1_8_8_0_3
  Dir = (0,0,1)
  DirMode = 0
  FaceMakerClass = Part::FaceMakerBullseye
  LengthFwd = 2
  LengthRev = 0
  Solid = true
  Symmetric = false
FEATURE [Part::Extrusion] Extrude035
  Base = -> path52401_71_2_4_9_4_2_0
  Dir = (0,0,1)
  DirMode = 0
  FaceMakerClass = Part::FaceMakerBullseye
  LengthFwd = 2
  LengthRev = 0
  Solid = true
  Symmetric = false
FEATURE [Part::Extrusion] Extrude036
  Base = -> path52401_7_8_1_8_2_3_5_0
  Dir = (0,0,1)
  DirMode = 0
  FaceMakerClass = Part::FaceMakerBullseye
  LengthFwd = 2
  LengthRev = 0
  Solid = true
  Symmetric = false
FEATURE [Part::Extrusion] Extrude037
  Base = -> path52377_0_5_0_4_2_4_4_3
  Dir = (0,0,1)
  DirMode = 0
  FaceMakerClass = Part::FaceMakerBullseye
  LengthFwd = 2
  LengthRev = 0
  Solid = true
  Symmetric = false
FEATURE [Part::Extrusion] Extrude038
  Base = -> path52456_0_5_5_7_7_7_7
  Dir = (0,0,1)
  DirMode = 0
  FaceMakerClass = Part::FaceMakerBullseye
  LengthFwd = 2
  LengthRev = 0
  Solid = true
  Symmetric = false
FEATURE [Part::Extrusion] Extrude039
  Base = -> path52377_09_3_1_8_2_9_7
  Dir = (0,0,1)
  DirMode = 0
  FaceMakerClass = Part::FaceMakerBullseye
  LengthFwd = 2
  LengthRev = 0
  Solid = true
  Symmetric = false
FEATURE [Part::Extrusion] Extrude040
  Base = -> path52401_71_2_4_9_2_6_0
  Dir = (0,0,1)
  DirMode = 0
  FaceMakerClass = Part::FaceMakerBullseye
  LengthFwd = 2
  LengthRev = 0
  Solid = true
  Symmetric = false
FEATURE [Part::Extrusion] Extrude041
  Base = -> path52401_7_8_1_8_2_31_56_74
  Dir = (0,0,1)
  DirMode = 0
  FaceMakerClass = Part::FaceMakerBullseye
  LengthFwd = 2
  LengthRev = 0
  Solid = true
  Symmetric = false
FEATURE [Part::Extrusion] Extrude042
  Base = -> path52377_0_5_0_4_2_41_4_91
  Dir = (0,0,1)
  DirMode = 0
  FaceMakerClass = Part::FaceMakerBullseye
  LengthFwd = 2
  LengthRev = 0
  Solid = true
  Symmetric = false
FEATURE [Part::Extrusion] Extrude043
  Base = -> path52456_0_5_5_7_4_40_0
  Dir = (0,0,1)
  DirMode = 0
  FaceMakerClass = Part::FaceMakerBullseye
  LengthFwd = 2
  LengthRev = 0
  Solid = true
  Symmetric = false
FEATURE [Part::Extrusion] Extrude044
  Base = -> path52377_09_3_1_8_2_4_0_1
  Dir = (0,0,1)
  DirMode = 0
  FaceMakerClass = Part::FaceMakerBullseye
  LengthFwd = 2
  LengthRev = 0
  Solid = true
  Symmetric = false
FEATURE [Part::Extrusion] Extrude045
  Base = -> path52401_71_2_4_9_2_9_9_55
  Dir = (0,0,1)
  DirMode = 0
  FaceMakerClass = Part::FaceMakerBullseye
  LengthFwd = 2
  LengthRev = 0
  Solid = true
  Symmetric = false
FEATURE [Part::Extrusion] Extrude046
  Base = -> path52401_7_8_1_8_2_31_5_9_4
  Dir = (0,0,1)
  DirMode = 0
  FaceMakerClass = Part::FaceMakerBullseye
  LengthFwd = 2
  LengthRev = 0
  Solid = true
  Symmetric = false
FEATURE [Part::Extrusion] Extrude047
  Base = -> path52377_0_5_0_4_2_41_0_4_8
  Dir = (0,0,1)
  DirMode = 0
  FaceMakerClass = Part::FaceMakerBullseye
  LengthFwd = 2
  LengthRev = 0
  Solid = true
  Symmetric = false
FEATURE [Part::Extrusion] Extrude048
  Base = -> path52456_0_5_5_7_4_4_8_02
  Dir = (0,0,1)
  DirMode = 0
  FaceMakerClass = Part::FaceMakerBullseye
  LengthFwd = 2
  LengthRev = 0
  Solid = true
  Symmetric = false
FEATURE [Part::Extrusion] Extrude049
  Base = -> path52377_09_3_1_8_8_0_4_7
  Dir = (0,0,1)
  DirMode = 0
  FaceMakerClass = Part::FaceMakerBullseye
  LengthFwd = 2
  LengthRev = 0
  Solid = true
  Symmetric = false
FEATURE [Part::Extrusion] Extrude050
  Base = -> path52401_71_2_4_9_4_2_2_1
  Dir = (0,0,1)
  DirMode = 0
  FaceMakerClass = Part::FaceMakerBullseye
  LengthFwd = 2
  LengthRev = 0
  Solid = true
  Symmetric = false
FEATURE [Part::Extrusion] Extrude051
  Base = -> path52401_7_8_1_8_2_3_5_3_8
  Dir = (0,0,1)
  DirMode = 0
  FaceMakerClass = Part::FaceMakerBullseye
  LengthFwd = 2
  LengthRev = 0
  Solid = true
  Symmetric = false
FEATURE [Part::Extrusion] Extrude052
  Base = -> path52377_0_5_0_4_2_4_4_8_3
  Dir = (0,0,1)
  DirMode = 0
  FaceMakerClass = Part::FaceMakerBullseye
  LengthFwd = 2
  LengthRev = 0
  Solid = true
  Symmetric = false
FEATURE [Part::Extrusion] Extrude053
  Base = -> path52456_0_5_5_7_7_7_1_3
  Dir = (0,0,1)
  DirMode = 0
  FaceMakerClass = Part::FaceMakerBullseye
  LengthFwd = 2
  LengthRev = 0
  Solid = true
  Symmetric = false
FEATURE [Part::Extrusion] Extrude054
  Base = -> path52377_09_3_1_8_2_9_5_3
  Dir = (0,0,1)
  DirMode = 0
  FaceMakerClass = Part::FaceMakerBullseye
  LengthFwd = 2
  LengthRev = 0
  Solid = true
  Symmetric = false
FEATURE [Part::Extrusion] Extrude055
  Base = -> path52401_71_2_4_9_2_6_3_64
  Dir = (0,0,1)
  DirMode = 0
  FaceMakerClass = Part::FaceMakerBullseye
  LengthFwd = 2
  LengthRev = 0
  Solid = true
  Symmetric = false
FEATURE [Part::Extrusion] Extrude056
  Base = -> path52401_7_8_1_8_2_31_56_1_9
  Dir = (0,0,1)
  DirMode = 0
  FaceMakerClass = Part::FaceMakerBullseye
  LengthFwd = 2
  LengthRev = 0
  Solid = true
  Symmetric = false
FEATURE [Part::Extrusion] Extrude057
  Base = -> path52377_0_5_0_4_2_41_4_8_1
  Dir = (0,0,1)
  DirMode = 0
  FaceMakerClass = Part::FaceMakerBullseye
  LengthFwd = 2
  LengthRev = 0
  Solid = true
  Symmetric = false
FEATURE [Part::Extrusion] Extrude058
  Base = -> path52456_0_5_5_7_4_40_5_0
  Dir = (0,0,1)
  DirMode = 0
  FaceMakerClass = Part::FaceMakerBullseye
  LengthFwd = 2
  LengthRev = 0
  Solid = true
  Symmetric = false
FEATURE [Part::Extrusion] Extrude059
  Base = -> path52377_09_3_1_8_2_4_0_5_8
  Dir = (0,0,1)
  DirMode = 0
  FaceMakerClass = Part::FaceMakerBullseye
  LengthFwd = 2
  LengthRev = 0
  Solid = true
  Symmetric = false
FEATURE [Part::Extrusion] Extrude060
  Base = -> path52401_71_2_4_9_2_9_9_5_64
  Dir = (0,0,1)
  DirMode = 0
  FaceMakerClass = Part::FaceMakerBullseye
  LengthFwd = 2
  LengthRev = 0
  Solid = true
  Symmetric = false
FEATURE [Part::Extrusion] Extrude061
  Base = -> path52401_7_8_1_8_2_31_5_9_9_9
  Dir = (0,0,1)
  DirMode = 0
  FaceMakerClass = Part::FaceMakerBullseye
  LengthFwd = 2
  LengthRev = 0
  Solid = true
  Symmetric = false
FEATURE [Part::Extrusion] Extrude062
  Base = -> path52377_0_5_0_4_2_41_0_4_1_4
  Dir = (0,0,1)
  DirMode = 0
  FaceMakerClass = Part::FaceMakerBullseye
  LengthFwd = 2
  LengthRev = 0
  Solid = true
  Symmetric = false
FEATURE [Part::Extrusion] Extrude063
  Base = -> path52456_0_5_5_7_4_4_8_5_4
  Dir = (0,0,1)
  DirMode = 0
  FaceMakerClass = Part::FaceMakerBullseye
  LengthFwd = 2
  LengthRev = 0
  Solid = true
  Symmetric = false
FEATURE [Part::Extrusion] Extrude064
  Base = -> path52377_09_3_1_8_8_0_4_5_6
  Dir = (0,0,1)
  DirMode = 0
  FaceMakerClass = Part::FaceMakerBullseye
  LengthFwd = 2
  LengthRev = 0
  Solid = true
  Symmetric = false
FEATURE [Part::Extrusion] Extrude065
  Base = -> path52401_71_2_4_9_4_2_2_8_5
  Dir = (0,0,1)
  DirMode = 0
  FaceMakerClass = Part::FaceMakerBullseye
  LengthFwd = 2
  LengthRev = 0
  Solid = true
  Symmetric = false
FEATURE [Part::Extrusion] Extrude066
  Base = -> path52401_7_8_1_8_2_3_5_3_4_2
  Dir = (0,0,1)
  DirMode = 0
  FaceMakerClass = Part::FaceMakerBullseye
  LengthFwd = 2
  LengthRev = 0
  Solid = true
  Symmetric = false
FEATURE [Part::Extrusion] Extrude067
  Base = -> path52377_0_5_0_4_2_4_4_8_9_1
  Dir = (0,0,1)
  DirMode = 0
  FaceMakerClass = Part::FaceMakerBullseye
  LengthFwd = 2
  LengthRev = 0
  Solid = true
  Symmetric = false
FEATURE [Part::Extrusion] Extrude068
  Base = -> path52456_0_5_5_7_7_7_1_7_8
  Dir = (0,0,1)
  DirMode = 0
  FaceMakerClass = Part::FaceMakerBullseye
  LengthFwd = 2
  LengthRev = 0
  Solid = true
  Symmetric = false
FEATURE [Part::Extrusion] Extrude069
  Base = -> path52377_09_3_1_8_2_9_5_4_8
  Dir = (0,0,1)
  DirMode = 0
  FaceMakerClass = Part::FaceMakerBullseye
  LengthFwd = 2
  LengthRev = 0
  Solid = true
  Symmetric = false
FEATURE [Part::Extrusion] Extrude070
  Base = -> path52401_71_2_4_9_2_6_3_6_9
  Dir = (0,0,1)
  DirMode = 0
  FaceMakerClass = Part::FaceMakerBullseye
  LengthFwd = 2
  LengthRev = 0
  Solid = true
  Symmetric = false
FEATURE [Part::Extrusion] Extrude071
  Base = -> path52401_7_8_1_8_2_31_56_1_3_7
  Dir = (0,0,1)
  DirMode = 0
  FaceMakerClass = Part::FaceMakerBullseye
  LengthFwd = 2
  LengthRev = 0
  Solid = true
  Symmetric = false
FEATURE [Part::Extrusion] Extrude072
  Base = -> path52377_0_5_0_4_2_41_4_8_8_6
  Dir = (0,0,1)
  DirMode = 0
  FaceMakerClass = Part::FaceMakerBullseye
  LengthFwd = 2
  LengthRev = 0
  Solid = true
  Symmetric = false
FEATURE [Part::Extrusion] Extrude073
  Base = -> path52456_0_5_5_7_4_40_5_1_45
  Dir = (0,0,1)
  DirMode = 0
  FaceMakerClass = Part::FaceMakerBullseye
  LengthFwd = 2
  LengthRev = 0
  Solid = true
  Symmetric = false
FEATURE [Part::Extrusion] Extrude074
  Base = -> path52377_09_3_1_8_2_4_0_5_0_4
  Dir = (0,0,1)
  DirMode = 0
  FaceMakerClass = Part::FaceMakerBullseye
  LengthFwd = 2
  LengthRev = 0
  Solid = true
  Symmetric = false
FEATURE [Part::Extrusion] Extrude075
  Base = -> path52401_71_2_4_9_2_9_9_5_6_8
  Dir = (0,0,1)
  DirMode = 0
  FaceMakerClass = Part::FaceMakerBullseye
  LengthFwd = 2
  LengthRev = 0
  Solid = true
  Symmetric = false
FEATURE [Part::Extrusion] Extrude076
  Base = -> path52401_7_8_1_8_2_31_5_9_9_0_0
  Dir = (0,0,1)
  DirMode = 0
  FaceMakerClass = Part::FaceMakerBullseye
  LengthFwd = 2
  LengthRev = 0
  Solid = true
  Symmetric = false
FEATURE [Part::Extrusion] Extrude077
  Base = -> path52377_0_5_0_4_2_41_0_4_1_8_44
  Dir = (0,0,1)
  DirMode = 0
  FaceMakerClass = Part::FaceMakerBullseye
  LengthFwd = 2
  LengthRev = 0
  Solid = true
  Symmetric = false
FEATURE [Part::Extrusion] Extrude078
  Base = -> path52456_0_5_5_7_4_4_8_5_8_8
  Dir = (0,0,1)
  DirMode = 0
  FaceMakerClass = Part::FaceMakerBullseye
  LengthFwd = 2
  LengthRev = 0
  Solid = true
  Symmetric = false
FEATURE [Part::Extrusion] Extrude079
  Base = -> path52377_09_3_1_8_8_0_4_5_8_91
  Dir = (0,0,1)
  DirMode = 0
  FaceMakerClass = Part::FaceMakerBullseye
  LengthFwd = 2
  LengthRev = 0
  Solid = true
  Symmetric = false
FEATURE [Part::Extrusion] Extrude080
  Base = -> path52401_71_2_4_9_4_2_2_8_7_5
  Dir = (0,0,1)
  DirMode = 0
  FaceMakerClass = Part::FaceMakerBullseye
  LengthFwd = 2
  LengthRev = 0
  Solid = true
  Symmetric = false
FEATURE [Part::Extrusion] Extrude081
  Base = -> path52401_7_8_1_8_2_3_5_3_4_4_44
  Dir = (0,0,1)
  DirMode = 0
  FaceMakerClass = Part::FaceMakerBullseye
  LengthFwd = 2
  LengthRev = 0
  Solid = true
  Symmetric = false
FEATURE [Part::Extrusion] Extrude082
  Base = -> path52377_0_5_0_4_2_4_4_8_9_2_9
  Dir = (0,0,1)
  DirMode = 0
  FaceMakerClass = Part::FaceMakerBullseye
  LengthFwd = 2
  LengthRev = 0
  Solid = true
  Symmetric = false
FEATURE [Part::Extrusion] Extrude083
  Base = -> path52456_0_5_5_7_7_7_1_7_0_2
  Dir = (0,0,1)
  DirMode = 0
  FaceMakerClass = Part::FaceMakerBullseye
  LengthFwd = 2
  LengthRev = 0
  Solid = true
  Symmetric = false
FEATURE [Part::Extrusion] Extrude084
  Base = -> path52377_09_3_1_8_2_9_5_4_9_5
  Dir = (0,0,1)
  DirMode = 0
  FaceMakerClass = Part::FaceMakerBullseye
  LengthFwd = 2
  LengthRev = 0
  Solid = true
  Symmetric = false
FEATURE [Part::Extrusion] Extrude085
  Base = -> path52401_71_2_4_9_2_6_3_6_8_5
  Dir = (0,0,1)
  DirMode = 0
  FaceMakerClass = Part::FaceMakerBullseye
  LengthFwd = 2
  LengthRev = 0
  Solid = true
  Symmetric = false
FEATURE [Part::Extrusion] Extrude086
  Base = -> path52401_7_8_1_8_2_31_56_1_3_0_2
  Dir = (0,0,1)
  DirMode = 0
  FaceMakerClass = Part::FaceMakerBullseye
  LengthFwd = 2
  LengthRev = 0
  Solid = true
  Symmetric = false
FEATURE [Part::Extrusion] Extrude087
  Base = -> path52377_0_5_0_4_2_41_4_8_8_0_5
  Dir = (0,0,1)
  DirMode = 0
  FaceMakerClass = Part::FaceMakerBullseye
  LengthFwd = 2
  LengthRev = 0
  Solid = true
  Symmetric = false
FEATURE [Part::Extrusion] Extrude088
  Base = -> path52456_0_5_5_7_4_40_5_1_5_56
  Dir = (0,0,1)
  DirMode = 0
  FaceMakerClass = Part::FaceMakerBullseye
  LengthFwd = 2
  LengthRev = 0
  Solid = true
  Symmetric = false
FEATURE [Part::Extrusion] Extrude089
  Base = -> path52377_09_3_1_8_2_4_0_5_0_2_7
  Dir = (0,0,1)
  DirMode = 0
  FaceMakerClass = Part::FaceMakerBullseye
  LengthFwd = 2
  LengthRev = 0
  Solid = true
  Symmetric = false
FEATURE [Part::Extrusion] Extrude090
  Base = -> path52401_71_2_4_9_2_9_9_5_6_2_6
  Dir = (0,0,1)
  DirMode = 0
  FaceMakerClass = Part::FaceMakerBullseye
  LengthFwd = 2
  LengthRev = 0
  Solid = true
  Symmetric = false
FEATURE [Part::Extrusion] Extrude091
  Base = -> path52401_7_8_1_8_2_31_5_9_9_0_7_2
  Dir = (0,0,1)
  DirMode = 0
  FaceMakerClass = Part::FaceMakerBullseye
  LengthFwd = 2
  LengthRev = 0
  Solid = true
  Symmetric = false
FEATURE [Part::Extrusion] Extrude092
  Base = -> path52377_0_5_0_4_2_41_0_4_1_8_4_4
  Dir = (0,0,1)
  DirMode = 0
  FaceMakerClass = Part::FaceMakerBullseye
  LengthFwd = 2
  LengthRev = 0
  Solid = true
  Symmetric = false
FEATURE [Part::Extrusion] Extrude093
  Base = -> path52456_0_5_5_7_4_4_8_5_8_0_3
  Dir = (0,0,1)
  DirMode = 0
  FaceMakerClass = Part::FaceMakerBullseye
  LengthFwd = 2
  LengthRev = 0
  Solid = true
  Symmetric = false
FEATURE [Part::Extrusion] Extrude094
  Base = -> path52377_09_3_1_8_8_0_4_5_8_9_1
  Dir = (0,0,1)
  DirMode = 0
  FaceMakerClass = Part::FaceMakerBullseye
  LengthFwd = 2
  LengthRev = 0
  Solid = true
  Symmetric = false
FEATURE [Part::Extrusion] Extrude095
  Base = -> path52401_71_2_4_9_4_2_2_8_7_6_2
  Dir = (0,0,1)
  DirMode = 0
  FaceMakerClass = Part::FaceMakerBullseye
  LengthFwd = 2
  LengthRev = 0
  Solid = true
  Symmetric = false
FEATURE [Part::Extrusion] Extrude096
  Base = -> path52401_7_8_1_8_2_3_5_3_4_4_8_8
  Dir = (0,0,1)
  DirMode = 0
  FaceMakerClass = Part::FaceMakerBullseye
  LengthFwd = 2
  LengthRev = 0
  Solid = true
  Symmetric = false
FEATURE [Part::Extrusion] Extrude097
  Base = -> path52377_0_5_0_4_2_4_4_8_9_2_0_5
  Dir = (0,0,1)
  DirMode = 0
  FaceMakerClass = Part::FaceMakerBullseye
  LengthFwd = 2
  LengthRev = 0
  Solid = true
  Symmetric = false
FEATURE [Part::Extrusion] Extrude098
  Base = -> path52456_0_5_5_7_7_7_1_7_0_0_6
  Dir = (0,0,1)
  DirMode = 0
  FaceMakerClass = Part::FaceMakerBullseye
  LengthFwd = 2
  LengthRev = 0
  Solid = true
  Symmetric = false
FEATURE [Part::Extrusion] Extrude099
  Base = -> circle37307_9_0_7_1
  Dir = (0,0,1)
  DirMode = 0
  FaceMakerClass = Part::FaceMakerBullseye
  LengthFwd = 2
  LengthRev = 0
  Solid = true
  Symmetric = false
FEATURE [Part::Extrusion] Extrude100
  Base = -> circle37313_0_5_2_6
  Dir = (0,0,1)
  DirMode = 0
  FaceMakerClass = Part::FaceMakerBullseye
  LengthFwd = 2
  LengthRev = 0
  Solid = true
  Symmetric = false
FEATURE [Part::Extrusion] Extrude101
  Base = -> path8_2
  Dir = (0,0,1)
  DirMode = 0
  FaceMakerClass = Part::FaceMakerBullseye
  LengthFwd = 2
  LengthRev = 0
  Solid = true
  Symmetric = false
FEATURE [Part::Extrusion] Extrude102
  Base = -> path4_1
  Dir = (0,0,1)
  DirMode = 0
  FaceMakerClass = Part::FaceMakerBullseye
  LengthFwd = 2
  LengthRev = 0
  Solid = true
  Symmetric = false
FEATURE [Part::Extrusion] Extrude103
  Base = -> path6_5
  Dir = (0,0,1)
  DirMode = 0
  FaceMakerClass = Part::FaceMakerBullseye
  LengthFwd = 2
  LengthRev = 0
  Solid = true
  Symmetric = false
FEATURE [Part::Extrusion] Extrude104
  Base = -> path2_5
  Dir = (0,0,1)
  DirMode = 0
  FaceMakerClass = Part::FaceMakerBullseye
  LengthFwd = 2
  LengthRev = 0
  Solid = true
  Symmetric = false
FEATURE [Part::Extrusion] Extrude105
  Base = -> path37931_6_3_3
  Dir = (0,0,1)
  DirMode = 0
  FaceMakerClass = Part::FaceMakerBullseye
  LengthFwd = 2
  LengthRev = 0
  Solid = true
  Symmetric = false
FEATURE [Part::Extrusion] Extrude106
  Base = -> path37937_8_1_8
  Dir = (0,0,1)
  DirMode = 0
  FaceMakerClass = Part::FaceMakerBullseye
  LengthFwd = 2
  LengthRev = 0
  Solid = true
  Symmetric = false
FEATURE [Part::Extrusion] Extrude107
  Base = -> rect117948_1_5_1_8
  Dir = (0,0,1)
  DirMode = 0
  FaceMakerClass = Part::FaceMakerBullseye
  LengthFwd = 2
  LengthRev = 0
  Solid = true
  Symmetric = false
FEATURE [Part::Extrusion] Extrude108
  Base = -> rect117948_2_0_8_5_8
  Dir = (0,0,1)
  DirMode = 0
  FaceMakerClass = Part::FaceMakerBullseye
  LengthFwd = 2
  LengthRev = 0
  Solid = true
  Symmetric = false
FEATURE [Part::Extrusion] Extrude109
  Base = -> path61609_4_5_7_9_4_80_0_8_78
  Dir = (0,0,1)
  DirMode = 0
  FaceMakerClass = Part::FaceMakerBullseye
  LengthFwd = 2
  LengthRev = 0
  Solid = true
  Symmetric = false
FEATURE [Part::Extrusion] Extrude110
  Base = -> path61609_4_5_7_9_4_80_0_3_8_68
  Dir = (0,0,1)
  DirMode = 0
  FaceMakerClass = Part::FaceMakerBullseye
  LengthFwd = 2
  LengthRev = 0
  Solid = true
  Symmetric = false
FEATURE [Part::Extrusion] Extrude111
  Base = -> path61609_4_5_7_9_4_80_0_3_8_6_79
  Dir = (0,0,1)
  DirMode = 0
  FaceMakerClass = Part::FaceMakerBullseye
  LengthFwd = 2
  LengthRev = 0
  Solid = true
  Symmetric = false
FEATURE [Part::Extrusion] Extrude112
  Base = -> path61609_4_5_7_9_4_80_0_8_3_5
  Dir = (0,0,1)
  DirMode = 0
  FaceMakerClass = Part::FaceMakerBullseye
  LengthFwd = 2
  LengthRev = 0
  Solid = true
  Symmetric = false
FEATURE [Part::Extrusion] Extrude113
  Base = -> path61609_4_5_7_9_4_80_0_3_8_9_3
  Dir = (0,0,1)
  DirMode = 0
  FaceMakerClass = Part::FaceMakerBullseye
  LengthFwd = 2
  LengthRev = 0
  Solid = true
  Symmetric = false
FEATURE [Part::Extrusion] Extrude114
  Base = -> path61609_4_5_7_9_4_80_0_3_8_6_1_2
  Dir = (0,0,1)
  DirMode = 0
  FaceMakerClass = Part::FaceMakerBullseye
  LengthFwd = 2
  LengthRev = 0
  Solid = true
  Symmetric = false
FEATURE [Part::Extrusion] Extrude115
  Base = -> path61609_4_5_7_9_4_80_0_8_7_0
  Dir = (0,0,1)
  DirMode = 0
  FaceMakerClass = Part::FaceMakerBullseye
  LengthFwd = 2
  LengthRev = 0
  Solid = true
  Symmetric = false
FEATURE [Part::Extrusion] Extrude116
  Base = -> path61609_4_5_7_9_4_80_0_3_8_91_1
  Dir = (0,0,1)
  DirMode = 0
  FaceMakerClass = Part::FaceMakerBullseye
  LengthFwd = 2
  LengthRev = 0
  Solid = true
  Symmetric = false
FEATURE [Part::Extrusion] Extrude117
  Base = -> path61609_4_5_7_9_4_80_0_3_8_6_3_6
  Dir = (0,0,1)
  DirMode = 0
  FaceMakerClass = Part::FaceMakerBullseye
  LengthFwd = 2
  LengthRev = 0
  Solid = true
  Symmetric = false
FEATURE [Part::Extrusion] Extrude118
  Base = -> path61609_4_5_7_9_4_80_0_8_8_6
  Dir = (0,0,1)
  DirMode = 0
  FaceMakerClass = Part::FaceMakerBullseye
  LengthFwd = 2
  LengthRev = 0
  Solid = true
  Symmetric = false
FEATURE [Part::Extrusion] Extrude119
  Base = -> path61609_4_5_7_9_4_80_0_3_8_0_9
  Dir = (0,0,1)
  DirMode = 0
  FaceMakerClass = Part::FaceMakerBullseye
  LengthFwd = 2
  LengthRev = 0
  Solid = true
  Symmetric = false
FEATURE [Part::Extrusion] Extrude120
  Base = -> path61609_4_5_7_9_4_80_0_3_8_6_7_8
  Dir = (0,0,1)
  DirMode = 0
  FaceMakerClass = Part::FaceMakerBullseye
  LengthFwd = 2
  LengthRev = 0
  Solid = true
  Symmetric = false
FEATURE [Part::Extrusion] Extrude121
  Base = -> path61609_4_5_7_9_4_80_0_8_2_6
  Dir = (0,0,1)
  DirMode = 0
  FaceMakerClass = Part::FaceMakerBullseye
  LengthFwd = 2
  LengthRev = 0
  Solid = true
  Symmetric = false
FEATURE [Part::Extrusion] Extrude122
  Base = -> path61609_4_5_7_9_4_80_0_3_8_60_6
  Dir = (0,0,1)
  DirMode = 0
  FaceMakerClass = Part::FaceMakerBullseye
  LengthFwd = 2
  LengthRev = 0
  Solid = true
  Symmetric = false
FEATURE [Part::Extrusion] Extrude123
  Base = -> path61609_4_5_7_9_4_80_0_3_8_6_4_2
  Dir = (0,0,1)
  DirMode = 0
  FaceMakerClass = Part::FaceMakerBullseye
  LengthFwd = 2
  LengthRev = 0
  Solid = true
  Symmetric = false
FEATURE [Part::Extrusion] Extrude124
  Base = -> path52377_09_3_5_7_6_7_3_2
  Dir = (0,0,1)
  DirMode = 0
  FaceMakerClass = Part::FaceMakerBullseye
  LengthFwd = 2
  LengthRev = 0
  Solid = true
  Symmetric = false
FEATURE [Part::Extrusion] Extrude125
  Base = -> path52401_71_2_5_9_2_77_3_4
  Dir = (0,0,1)
  DirMode = 0
  FaceMakerClass = Part::FaceMakerBullseye
  LengthFwd = 2
  LengthRev = 0
  Solid = true
  Symmetric = false
FEATURE [Part::Extrusion] Extrude126
  Base = -> path52401_7_8_1_1_7_3_9_0_7
  Dir = (0,0,1)
  DirMode = 0
  FaceMakerClass = Part::FaceMakerBullseye
  LengthFwd = 2
  LengthRev = 0
  Solid = true
  Symmetric = false
FEATURE [Part::Extrusion] Extrude127
  Base = -> path52377_0_5_0_1_9_1_5_5_6
  Dir = (0,0,1)
  DirMode = 0
  FaceMakerClass = Part::FaceMakerBullseye
  LengthFwd = 2
  LengthRev = 0
  Solid = true
  Symmetric = false
FEATURE [Part::Extrusion] Extrude128
  Base = -> path52456_0_5_2_2_2_3_5_8
  Dir = (0,0,1)
  DirMode = 0
  FaceMakerClass = Part::FaceMakerBullseye
  LengthFwd = 2
  LengthRev = 0
  Solid = true
  Symmetric = false
FEATURE [Part::Extrusion] Extrude129
  Base = -> path52377_09_3_5_7_6_0_0_2_2
  Dir = (0,0,1)
  DirMode = 0
  FaceMakerClass = Part::FaceMakerBullseye
  LengthFwd = 2
  LengthRev = 0
  Solid = true
  Symmetric = false
FEATURE [Part::Extrusion] Extrude130
  Base = -> path52401_71_2_5_9_2_7_5_4_9
  Dir = (0,0,1)
  DirMode = 0
  FaceMakerClass = Part::FaceMakerBullseye
  LengthFwd = 2
  LengthRev = 0
  Solid = true
  Symmetric = false
FEATURE [Part::Extrusion] Extrude131
  Base = -> path52401_7_8_1_1_7_3_8_4_4_6
  Dir = (0,0,1)
  DirMode = 0
  FaceMakerClass = Part::FaceMakerBullseye
  LengthFwd = 2
  LengthRev = 0
  Solid = true
  Symmetric = false
FEATURE [Part::Extrusion] Extrude132
  Base = -> path52377_0_5_0_1_9_1_0_6_9_1
  Dir = (0,0,1)
  DirMode = 0
  FaceMakerClass = Part::FaceMakerBullseye
  LengthFwd = 2
  LengthRev = 0
  Solid = true
  Symmetric = false
FEATURE [Part::Extrusion] Extrude133
  Base = -> path52456_0_5_2_2_2_9_9_3_1
  Dir = (0,0,1)
  DirMode = 0
  FaceMakerClass = Part::FaceMakerBullseye
  LengthFwd = 2
  LengthRev = 0
  Solid = true
  Symmetric = false
FEATURE [Part::Extrusion] Extrude134
  Base = -> path52377_09_3_5_7_6_6_7_9_0
  Dir = (0,0,1)
  DirMode = 0
  FaceMakerClass = Part::FaceMakerBullseye
  LengthFwd = 2
  LengthRev = 0
  Solid = true
  Symmetric = false
FEATURE [Part::Extrusion] Extrude135
  Base = -> path52401_71_2_5_9_2_1_4_5_2
  Dir = (0,0,1)
  DirMode = 0
  FaceMakerClass = Part::FaceMakerBullseye
  LengthFwd = 2
  LengthRev = 0
  Solid = true
  Symmetric = false
FEATURE [Part::Extrusion] Extrude136
  Base = -> path52401_7_8_1_1_7_3_1_9_1_9
  Dir = (0,0,1)
  DirMode = 0
  FaceMakerClass = Part::FaceMakerBullseye
  LengthFwd = 2
  LengthRev = 0
  Solid = true
  Symmetric = false
FEATURE [Part::Extrusion] Extrude137
  Base = -> path52377_0_5_0_1_9_1_3_9_3_6
  Dir = (0,0,1)
  DirMode = 0
  FaceMakerClass = Part::FaceMakerBullseye
  LengthFwd = 2
  LengthRev = 0
  Solid = true
  Symmetric = false
FEATURE [Part::Extrusion] Extrude138
  Base = -> path52456_0_5_2_2_2_5_8_5_5
  Dir = (0,0,1)
  DirMode = 0
  FaceMakerClass = Part::FaceMakerBullseye
  LengthFwd = 2
  LengthRev = 0
  Solid = true
  Symmetric = false
FEATURE [Part::Extrusion] Extrude139
  Base = -> path52377_09_3_5_7_6_4_7_2_2
  Dir = (0,0,1)
  DirMode = 0
  FaceMakerClass = Part::FaceMakerBullseye
  LengthFwd = 2
  LengthRev = 0
  Solid = true
  Symmetric = false
FEATURE [Part::Extrusion] Extrude140
  Base = -> path52401_71_2_5_9_2_8_0_6_1
  Dir = (0,0,1)
  DirMode = 0
  FaceMakerClass = Part::FaceMakerBullseye
  LengthFwd = 2
  LengthRev = 0
  Solid = true
  Symmetric = false
FEATURE [Part::Extrusion] Extrude141
  Base = -> path52401_7_8_1_1_7_3_6_7_6_3
  Dir = (0,0,1)
  DirMode = 0
  FaceMakerClass = Part::FaceMakerBullseye
  LengthFwd = 2
  LengthRev = 0
  Solid = true
  Symmetric = false
FEATURE [Part::Extrusion] Extrude142
  Base = -> path52377_0_5_0_1_9_1_4_7_5_3
  Dir = (0,0,1)
  DirMode = 0
  FaceMakerClass = Part::FaceMakerBullseye
  LengthFwd = 2
  LengthRev = 0
  Solid = true
  Symmetric = false
FEATURE [Part::Extrusion] Extrude143
  Base = -> path52456_0_5_2_2_2_7_4_6_3
  Dir = (0,0,1)
  DirMode = 0
  FaceMakerClass = Part::FaceMakerBullseye
  LengthFwd = 2
  LengthRev = 0
  Solid = true
  Symmetric = false
FEATURE [Part::Extrusion] Extrude144
  Base = -> path61609_4_5_7_9_4_80_0_8_2_8_3_3
  Dir = (0,0,1)
  DirMode = 0
  FaceMakerClass = Part::FaceMakerBullseye
  LengthFwd = 2
  LengthRev = 0
  Solid = true
  Symmetric = false
FEATURE [Part::Extrusion] Extrude145
  Base = -> path61609_4_5_7_9_4_80_0_8_2_8_3_6_9
  Dir = (0,0,1)
  DirMode = 0
  FaceMakerClass = Part::FaceMakerBullseye
  LengthFwd = 2
  LengthRev = 0
  Solid = true
  Symmetric = false
FEATURE [Part::Extrusion] Extrude146
  Base = -> path61609_4_5_7_9_4_80_0_8_2_8_3_69_9
  Dir = (0,0,1)
  DirMode = 0
  FaceMakerClass = Part::FaceMakerBullseye
  LengthFwd = 2
  LengthRev = 0
  Solid = true
  Symmetric = false
FEATURE [Part::Extrusion] Extrude147
  Base = -> path61609_4_5_7_9_4_80_0_8_2_8_3_7_7
  Dir = (0,0,1)
  DirMode = 0
  FaceMakerClass = Part::FaceMakerBullseye
  LengthFwd = 2
  LengthRev = 0
  Solid = true
  Symmetric = false
FEATURE [Part::MultiFuse] Fusion001  label="wells_left"
  Placement = pos=(0,0,1) rot=(0,0,1;0rad)
  Shapes = -> [Extrude012,Extrude013,Extrude014,Extrude015,Extrude016,Extrude017,Extrude018,Extrude019,Extrude020,Extrude021,Extrude022,Extrude023,Extrude024,Extrude025,Extrude026,Extrude027,Extrude028,Extrude029,Extrude030,Extrude031,Extrude032,Extrude033,Extrude034,Extrude035,Extrude036,Extrude037,Extrude038,Extrude039,Extrude040,Extrude041,Extrude042,Extrude043,Extrude044,Extrude045,Extrude046,Extrude047,+100 more]
FEATURE [Part::Feature] path44149_5_004
  shape: bbox 139.5 x 94.73 x 2e-07 mm, 0 faces, 0 solids (baked)
FEATURE [Part::Extrusion] Extrude149  label="inner_right"
  Base = -> path44149_5_004
  Dir = (0,0,1)
  DirMode = 0
  FaceMakerClass = Part::FaceMakerBullseye
  LengthFwd = 0.8
  LengthRev = 0
  Placement = pos=(0,0,3) rot=(0,0,1;0rad)
  Solid = true
  Symmetric = false
FEATURE [Part::Feature] path44149_5_005
  shape: bbox 145.5 x 102.4 x 2e-07 mm, 0 faces, 0 solids (baked)
FEATURE [Part::Extrusion] Extrude148  label="bounds_right"
  Base = -> path44149_5_005
  Dir = (0,0,1)
  DirMode = 0
  FaceMakerClass = Part::FaceMakerBullseye
  LengthFwd = 2.8
  LengthRev = 0
  Placement = pos=(0,0,1) rot=(0,0,1;0rad)
  Solid = true
  Symmetric = false
FEATURE [Part::Feature] path52377_09_3_1_8_87_9
  Placement = pos=(-112.198,-129.883,0) rot=(0,0,1;0rad)
  shape: bbox 1.877 x 2.052 x 2e-07 mm, 0 faces, 0 solids (baked)
FEATURE [Part::Feature] path52401_71_2_4_9_8_2
  Placement = pos=(-111.698,-133.683,0) rot=(0,0,1;0rad)
  shape: bbox 2.208 x 2.415 x 2e-07 mm, 0 faces, 0 solids (baked)
FEATURE [Part::Feature] path52401_7_8_1_8_2_30_6
  Placement = pos=(-106.698,-135.783,0) rot=(0,0,1;0rad)
  shape: bbox 2.208 x 2.415 x 2e-07 mm, 0 faces, 0 solids (baked)
FEATURE [Part::Feature] path52377_0_5_0_4_2_3_6
  Placement = pos=(-101.198,-129.883,0) rot=(0,0,1;0rad)
  shape: bbox 1.877 x 2.052 x 2e-07 mm, 0 faces, 0 solids (baked)
FEATURE [Part::Feature] path52456_0_5_5_7_86_8
  Placement = pos=(-106.698,-129.883,0) rot=(0,0,1;0rad)
  shape: bbox 3.787 x 4.141 x 2e-07 mm, 0 faces, 0 solids (baked)
FEATURE [Part::Feature] path52377_09_3_1_8_8_2_0
  Placement = pos=(-112.198,-112.884,0) rot=(0,0,1;0rad)
  shape: bbox 1.877 x 2.052 x 2e-07 mm, 0 faces, 0 solids (baked)
FEATURE [Part::Feature] path52401_71_2_4_9_4_5_7
  Placement = pos=(-111.698,-116.684,0) rot=(0,0,1;0rad)
  shape: bbox 2.208 x 2.415 x 2e-07 mm, 0 faces, 0 solids (baked)
FEATURE [Part::Feature] path52401_7_8_1_8_2_3_11_7
  Placement = pos=(-106.698,-118.784,0) rot=(0,0,1;0rad)
  shape: bbox 2.208 x 2.415 x 2e-07 mm, 0 faces, 0 solids (baked)
FEATURE [Part::Feature] path52377_0_5_0_4_2_4_5_9
  Placement = pos=(-101.198,-112.884,0) rot=(0,0,1;0rad)
  shape: bbox 1.877 x 2.052 x 2e-07 mm, 0 faces, 0 solids (baked)
FEATURE [Part::Feature] path52456_0_5_5_7_7_0_9
  Placement = pos=(-106.698,-112.884,0) rot=(0,0,1;0rad)
  shape: bbox 3.787 x 4.141 x 2e-07 mm, 0 faces, 0 solids (baked)
FEATURE [Part::Feature] path52377_09_3_1_8_2_3_2
  Placement = pos=(-130.198,-121.383,0) rot=(0,0,1;0rad)
  shape: bbox 1.877 x 2.052 x 2e-07 mm, 0 faces, 0 solids (baked)
FEATURE [Part::Feature] path52401_71_2_4_9_2_39_0
  Placement = pos=(-129.698,-125.183,0) rot=(0,0,1;0rad)
  shape: bbox 2.208 x 2.415 x 2e-07 mm, 0 faces, 0 solids (baked)
FEATURE [Part::Feature] path52401_7_8_1_8_2_31_2_2
  Placement = pos=(-124.698,-127.283,0) rot=(0,0,1;0rad)
  shape: bbox 2.208 x 2.415 x 2e-07 mm, 0 faces, 0 solids (baked)
FEATURE [Part::Feature] path52377_0_5_0_4_2_41_1_6
  Placement = pos=(-119.198,-121.383,0) rot=(0,0,1;0rad)
  shape: bbox 1.877 x 2.052 x 2e-07 mm, 0 faces, 0 solids (baked)
FEATURE [Part::Feature] path52456_0_5_5_7_4_2_7
  Placement = pos=(-124.698,-121.383,0) rot=(0,0,1;0rad)
  shape: bbox 3.787 x 4.141 x 2e-07 mm, 0 faces, 0 solids (baked)
FEATURE [Part::Feature] path52377_09_3_1_8_2_4_7_4
  Placement = pos=(-130.198,-138.383,0) rot=(0,0,1;0rad)
  shape: bbox 1.877 x 2.052 x 2e-07 mm, 0 faces, 0 solids (baked)
FEATURE [Part::Feature] path52401_71_2_4_9_2_9_8_3
  Placement = pos=(-129.698,-142.183,0) rot=(0,0,1;0rad)
  shape: bbox 2.208 x 2.415 x 2e-07 mm, 0 faces, 0 solids (baked)
FEATURE [Part::Feature] path52401_7_8_1_8_2_31_5_4_3
  Placement = pos=(-124.698,-144.283,0) rot=(0,0,1;0rad)
  shape: bbox 2.208 x 2.415 x 2e-07 mm, 0 faces, 0 solids (baked)
FEATURE [Part::Feature] path52377_0_5_0_4_2_41_0_0_8
  Placement = pos=(-119.198,-138.383,0) rot=(0,0,1;0rad)
  shape: bbox 1.877 x 2.052 x 2e-07 mm, 0 faces, 0 solids (baked)
FEATURE [Part::Feature] path52456_0_5_5_7_4_4_1_2
  Placement = pos=(-124.698,-138.383,0) rot=(0,0,1;0rad)
  shape: bbox 3.787 x 4.141 x 2e-07 mm, 0 faces, 0 solids (baked)
FEATURE [Part::Feature] path52377_09_3_1_8_8_0_3_5
  Placement = pos=(-130.198,-104.384,0) rot=(0,0,1;0rad)
  shape: bbox 1.877 x 2.052 x 2e-07 mm, 0 faces, 0 solids (baked)
FEATURE [Part::Feature] path52401_71_2_4_9_4_2_0_8
  Placement = pos=(-129.698,-108.184,0) rot=(0,0,1;0rad)
  shape: bbox 2.208 x 2.415 x 2e-07 mm, 0 faces, 0 solids (baked)
FEATURE [Part::Feature] path52401_7_8_1_8_2_3_5_0_1
  Placement = pos=(-124.698,-110.284,0) rot=(0,0,1;0rad)
  shape: bbox 2.208 x 2.415 x 2e-07 mm, 0 faces, 0 solids (baked)
FEATURE [Part::Feature] path52377_0_5_0_4_2_4_4_3_3
  Placement = pos=(-119.198,-104.384,0) rot=(0,0,1;0rad)
  shape: bbox 1.877 x 2.052 x 2e-07 mm, 0 faces, 0 solids (baked)
FEATURE [Part::Feature] path52456_0_5_5_7_7_7_7_4
  Placement = pos=(-124.698,-104.384,0) rot=(0,0,1;0rad)
  shape: bbox 3.787 x 4.141 x 2e-07 mm, 0 faces, 0 solids (baked)
FEATURE [Part::Feature] path52377_09_3_1_8_2_9_7_8
  Placement = pos=(-148.198,-109.383,0) rot=(0,0,1;0rad)
  shape: bbox 1.877 x 2.052 x 2e-07 mm, 0 faces, 0 solids (baked)
FEATURE [Part::Feature] path52401_71_2_4_9_2_6_0_6
  Placement = pos=(-147.698,-113.183,0) rot=(0,0,1;0rad)
  shape: bbox 2.208 x 2.415 x 2e-07 mm, 0 faces, 0 solids (baked)
FEATURE [Part::Feature] path52401_7_8_1_8_2_31_56_74_0
  Placement = pos=(-142.698,-115.283,0) rot=(0,0,1;0rad)
  shape: bbox 2.208 x 2.415 x 2e-07 mm, 0 faces, 0 solids (baked)
FEATURE [Part::Feature] path52377_0_5_0_4_2_41_4_91_1
  Placement = pos=(-137.198,-109.383,0) rot=(0,0,1;0rad)
  shape: bbox 1.877 x 2.052 x 2e-07 mm, 0 faces, 0 solids (baked)
FEATURE [Part::Feature] path52456_0_5_5_7_4_40_0_2
  Placement = pos=(-142.698,-109.383,0) rot=(0,0,1;0rad)
  shape: bbox 3.787 x 4.141 x 2e-07 mm, 0 faces, 0 solids (baked)
FEATURE [Part::Feature] path52377_09_3_1_8_2_4_0_1_3
  Placement = pos=(-148.198,-126.383,0) rot=(0,0,1;0rad)
  shape: bbox 1.877 x 2.052 x 2e-07 mm, 0 faces, 0 solids (baked)
FEATURE [Part::Feature] path52401_71_2_4_9_2_9_9_55_5
  Placement = pos=(-147.698,-130.183,0) rot=(0,0,1;0rad)
  shape: bbox 2.208 x 2.415 x 2e-07 mm, 0 faces, 0 solids (baked)
FEATURE [Part::Feature] path52401_7_8_1_8_2_31_5_9_4_8
  Placement = pos=(-142.698,-132.283,0) rot=(0,0,1;0rad)
  shape: bbox 2.208 x 2.415 x 2e-07 mm, 0 faces, 0 solids (baked)
FEATURE [Part::Feature] path52377_0_5_0_4_2_41_0_4_8_5
  Placement = pos=(-137.198,-126.383,0) rot=(0,0,1;0rad)
  shape: bbox 1.877 x 2.052 x 2e-07 mm, 0 faces, 0 solids (baked)
FEATURE [Part::Feature] path52456_0_5_5_7_4_4_8_02_7
  Placement = pos=(-142.698,-126.383,0) rot=(0,0,1;0rad)
  shape: bbox 3.787 x 4.141 x 2e-07 mm, 0 faces, 0 solids (baked)
FEATURE [Part::Feature] path52377_09_3_1_8_8_0_4_7_0
  Placement = pos=(-148.198,-92.3836,0) rot=(0,0,1;0rad)
  shape: bbox 1.877 x 2.052 x 2e-07 mm, 0 faces, 0 solids (baked)
FEATURE [Part::Feature] path52401_71_2_4_9_4_2_2_1_9
  Placement = pos=(-147.698,-96.1835,0) rot=(0,0,1;0rad)
  shape: bbox 2.208 x 2.415 x 2e-07 mm, 0 faces, 0 solids (baked)
FEATURE [Part::Feature] path52401_7_8_1_8_2_3_5_3_8_2
  Placement = pos=(-142.698,-98.2836,0) rot=(0,0,1;0rad)
  shape: bbox 2.208 x 2.415 x 2e-07 mm, 0 faces, 0 solids (baked)
FEATURE [Part::Feature] path52377_0_5_0_4_2_4_4_8_3_2
  Placement = pos=(-137.198,-92.3836,0) rot=(0,0,1;0rad)
  shape: bbox 1.877 x 2.052 x 2e-07 mm, 0 faces, 0 solids (baked)
FEATURE [Part::Feature] path52456_0_5_5_7_7_7_1_3_6
  Placement = pos=(-142.698,-92.3836,0) rot=(0,0,1;0rad)
  shape: bbox 3.787 x 4.141 x 2e-07 mm, 0 faces, 0 solids (baked)
FEATURE [Part::Feature] path52377_09_3_1_8_2_9_5_3_6
  Placement = pos=(-166.198,-104.383,0) rot=(0,0,1;0rad)
  shape: bbox 1.877 x 2.052 x 2e-07 mm, 0 faces, 0 solids (baked)
FEATURE [Part::Feature] path52401_71_2_4_9_2_6_3_64_9
  Placement = pos=(-165.698,-108.183,0) rot=(0,0,1;0rad)
  shape: bbox 2.208 x 2.415 x 2e-07 mm, 0 faces, 0 solids (baked)
FEATURE [Part::Feature] path52401_7_8_1_8_2_31_56_1_9_8
  Placement = pos=(-160.698,-110.283,0) rot=(0,0,1;0rad)
  shape: bbox 2.208 x 2.415 x 2e-07 mm, 0 faces, 0 solids (baked)
FEATURE [Part::Feature] path52377_0_5_0_4_2_41_4_8_1_3
  Placement = pos=(-155.198,-104.383,0) rot=(0,0,1;0rad)
  shape: bbox 1.877 x 2.052 x 2e-07 mm, 0 faces, 0 solids (baked)
FEATURE [Part::Feature] path52456_0_5_5_7_4_40_5_0_6
  Placement = pos=(-160.698,-104.383,0) rot=(0,0,1;0rad)
  shape: bbox 3.787 x 4.141 x 2e-07 mm, 0 faces, 0 solids (baked)
FEATURE [Part::Feature] path52377_09_3_1_8_2_4_0_5_8_4
  Placement = pos=(-166.198,-121.383,0) rot=(0,0,1;0rad)
  shape: bbox 1.877 x 2.052 x 2e-07 mm, 0 faces, 0 solids (baked)
FEATURE [Part::Feature] path52401_71_2_4_9_2_9_9_5_64_7
  Placement = pos=(-165.698,-125.183,0) rot=(0,0,1;0rad)
  shape: bbox 2.208 x 2.415 x 2e-07 mm, 0 faces, 0 solids (baked)
FEATURE [Part::Feature] path52401_7_8_1_8_2_31_5_9_9_9_3
  Placement = pos=(-160.698,-127.283,0) rot=(0,0,1;0rad)
  shape: bbox 2.208 x 2.415 x 2e-07 mm, 0 faces, 0 solids (baked)
FEATURE [Part::Feature] path52377_0_5_0_4_2_41_0_4_1_4_0
  Placement = pos=(-155.198,-121.383,0) rot=(0,0,1;0rad)
  shape: bbox 1.877 x 2.052 x 2e-07 mm, 0 faces, 0 solids (baked)
FEATURE [Part::Feature] path52456_0_5_5_7_4_4_8_5_4_4
  Placement = pos=(-160.698,-121.383,0) rot=(0,0,1;0rad)
  shape: bbox 3.787 x 4.141 x 2e-07 mm, 0 faces, 0 solids (baked)
FEATURE [Part::Feature] path52377_09_3_1_8_8_0_4_5_6_9
  Placement = pos=(-166.198,-87.3836,0) rot=(0,0,1;0rad)
  shape: bbox 1.877 x 2.052 x 2e-07 mm, 0 faces, 0 solids (baked)
FEATURE [Part::Feature] path52401_71_2_4_9_4_2_2_8_5_1
  Placement = pos=(-165.698,-91.1835,0) rot=(0,0,1;0rad)
  shape: bbox 2.208 x 2.415 x 2e-07 mm, 0 faces, 0 solids (baked)
FEATURE [Part::Feature] path52401_7_8_1_8_2_3_5_3_4_2_3
  Placement = pos=(-160.698,-93.2836,0) rot=(0,0,1;0rad)
  shape: bbox 2.208 x 2.415 x 2e-07 mm, 0 faces, 0 solids (baked)
FEATURE [Part::Feature] path52377_0_5_0_4_2_4_4_8_9_1_6
  Placement = pos=(-155.198,-87.3836,0) rot=(0,0,1;0rad)
  shape: bbox 1.877 x 2.052 x 2e-07 mm, 0 faces, 0 solids (baked)
FEATURE [Part::Feature] path52456_0_5_5_7_7_7_1_7_8_9
  Placement = pos=(-160.698,-87.3836,0) rot=(0,0,1;0rad)
  shape: bbox 3.787 x 4.141 x 2e-07 mm, 0 faces, 0 solids (baked)
FEATURE [Part::Feature] path52377_09_3_1_8_2_9_5_4_8_4
  Placement = pos=(-184.198,-109.383,0) rot=(0,0,1;0rad)
  shape: bbox 1.877 x 2.052 x 2e-07 mm, 0 faces, 0 solids (baked)
FEATURE [Part::Feature] path52401_71_2_4_9_2_6_3_6_9_9
  Placement = pos=(-183.698,-113.183,0) rot=(0,0,1;0rad)
  shape: bbox 2.208 x 2.415 x 2e-07 mm, 0 faces, 0 solids (baked)
FEATURE [Part::Feature] path52401_7_8_1_8_2_31_56_1_3_7_7
  Placement = pos=(-178.698,-115.283,0) rot=(0,0,1;0rad)
  shape: bbox 2.208 x 2.415 x 2e-07 mm, 0 faces, 0 solids (baked)
FEATURE [Part::Feature] path52377_0_5_0_4_2_41_4_8_8_6_8
  Placement = pos=(-173.198,-109.383,0) rot=(0,0,1;0rad)
  shape: bbox 1.877 x 2.052 x 2e-07 mm, 0 faces, 0 solids (baked)
FEATURE [Part::Feature] path52456_0_5_5_7_4_40_5_1_45_0
  Placement = pos=(-178.698,-109.383,0) rot=(0,0,1;0rad)
  shape: bbox 3.787 x 4.141 x 2e-07 mm, 0 faces, 0 solids (baked)
FEATURE [Part::Feature] path52377_09_3_1_8_2_4_0_5_0_4_8
  Placement = pos=(-184.198,-126.383,0) rot=(0,0,1;0rad)
  shape: bbox 1.877 x 2.052 x 2e-07 mm, 0 faces, 0 solids (baked)
FEATURE [Part::Feature] path52401_71_2_4_9_2_9_9_5_6_8_4
  Placement = pos=(-183.698,-130.183,0) rot=(0,0,1;0rad)
  shape: bbox 2.208 x 2.415 x 2e-07 mm, 0 faces, 0 solids (baked)
FEATURE [Part::Feature] path52401_7_8_1_8_2_31_5_9_9_0_0_2
  Placement = pos=(-178.698,-132.283,0) rot=(0,0,1;0rad)
  shape: bbox 2.208 x 2.415 x 2e-07 mm, 0 faces, 0 solids (baked)
FEATURE [Part::Feature] path52377_0_5_0_4_2_41_0_4_1_8_44_4
  Placement = pos=(-173.198,-126.383,0) rot=(0,0,1;0rad)
  shape: bbox 1.877 x 2.052 x 2e-07 mm, 0 faces, 0 solids (baked)
FEATURE [Part::Feature] path52456_0_5_5_7_4_4_8_5_8_8_3
  Placement = pos=(-178.698,-126.383,0) rot=(0,0,1;0rad)
  shape: bbox 3.787 x 4.141 x 2e-07 mm, 0 faces, 0 solids (baked)
FEATURE [Part::Feature] path52377_09_3_1_8_8_0_4_5_8_91_9
  Placement = pos=(-184.198,-92.3836,0) rot=(0,0,1;0rad)
  shape: bbox 1.877 x 2.052 x 2e-07 mm, 0 faces, 0 solids (baked)
FEATURE [Part::Feature] path52401_71_2_4_9_4_2_2_8_7_5_0
  Placement = pos=(-183.698,-96.1835,0) rot=(0,0,1;0rad)
  shape: bbox 2.208 x 2.415 x 2e-07 mm, 0 faces, 0 solids (baked)
FEATURE [Part::Feature] path52401_7_8_1_8_2_3_5_3_4_4_44_4
  Placement = pos=(-178.698,-98.2836,0) rot=(0,0,1;0rad)
  shape: bbox 2.208 x 2.415 x 2e-07 mm, 0 faces, 0 solids (baked)
FEATURE [Part::Feature] path52377_0_5_0_4_2_4_4_8_9_2_9_3
  Placement = pos=(-173.198,-92.3836,0) rot=(0,0,1;0rad)
  shape: bbox 1.877 x 2.052 x 2e-07 mm, 0 faces, 0 solids (baked)
FEATURE [Part::Feature] path52456_0_5_5_7_7_7_1_7_0_2_7
  Placement = pos=(-178.698,-92.3836,0) rot=(0,0,1;0rad)
  shape: bbox 3.787 x 4.141 x 2e-07 mm, 0 faces, 0 solids (baked)
FEATURE [Part::Feature] path52377_09_3_1_8_2_9_5_4_9_5_7
  Placement = pos=(-202.198,-111.383,0) rot=(0,0,1;0rad)
  shape: bbox 1.877 x 2.052 x 2e-07 mm, 0 faces, 0 solids (baked)
FEATURE [Part::Feature] path52401_71_2_4_9_2_6_3_6_8_5_8
  Placement = pos=(-201.698,-115.183,0) rot=(0,0,1;0rad)
  shape: bbox 2.208 x 2.415 x 2e-07 mm, 0 faces, 0 solids (baked)
FEATURE [Part::Feature] path52401_7_8_1_8_2_31_56_1_3_0_2_9
  Placement = pos=(-196.698,-117.283,0) rot=(0,0,1;0rad)
  shape: bbox 2.208 x 2.415 x 2e-07 mm, 0 faces, 0 solids (baked)
FEATURE [Part::Feature] path52377_0_5_0_4_2_41_4_8_8_0_5_5
  Placement = pos=(-191.198,-111.383,0) rot=(0,0,1;0rad)
  shape: bbox 1.877 x 2.052 x 2e-07 mm, 0 faces, 0 solids (baked)
FEATURE [Part::Feature] path52456_0_5_5_7_4_40_5_1_5_56_6
  Placement = pos=(-196.698,-111.383,0) rot=(0,0,1;0rad)
  shape: bbox 3.787 x 4.141 x 2e-07 mm, 0 faces, 0 solids (baked)
FEATURE [Part::Feature] path52377_09_3_1_8_2_4_0_5_0_2_7_9
  Placement = pos=(-202.198,-128.383,0) rot=(0,0,1;0rad)
  shape: bbox 1.877 x 2.052 x 2e-07 mm, 0 faces, 0 solids (baked)
FEATURE [Part::Feature] path52401_71_2_4_9_2_9_9_5_6_2_6_5
  Placement = pos=(-201.698,-132.183,0) rot=(0,0,1;0rad)
  shape: bbox 2.208 x 2.415 x 2e-07 mm, 0 faces, 0 solids (baked)
FEATURE [Part::Feature] path52401_7_8_1_8_2_31_5_9_9_0_7_2_4
  Placement = pos=(-196.698,-134.283,0) rot=(0,0,1;0rad)
  shape: bbox 2.208 x 2.415 x 2e-07 mm, 0 faces, 0 solids (baked)
FEATURE [Part::Feature] path52377_0_5_0_4_2_41_0_4_1_8_4_4_5
  Placement = pos=(-191.198,-128.383,0) rot=(0,0,1;0rad)
  shape: bbox 1.877 x 2.052 x 2e-07 mm, 0 faces, 0 solids (baked)
FEATURE [Part::Feature] path52456_0_5_5_7_4_4_8_5_8_0_3_1
  Placement = pos=(-196.698,-128.383,0) rot=(0,0,1;0rad)
  shape: bbox 3.787 x 4.141 x 2e-07 mm, 0 faces, 0 solids (baked)
FEATURE [Part::Feature] path52377_09_3_1_8_8_0_4_5_8_9_1_3
  Placement = pos=(-202.198,-94.3836,0) rot=(0,0,1;0rad)
  shape: bbox 1.877 x 2.052 x 2e-07 mm, 0 faces, 0 solids (baked)
FEATURE [Part::Feature] path52401_71_2_4_9_4_2_2_8_7_6_2_4
  Placement = pos=(-201.698,-98.1836,0) rot=(0,0,1;0rad)
  shape: bbox 2.208 x 2.415 x 2e-07 mm, 0 faces, 0 solids (baked)
FEATURE [Part::Feature] path52401_7_8_1_8_2_3_5_3_4_4_8_8_9
  Placement = pos=(-196.698,-100.284,0) rot=(0,0,1;0rad)
  shape: bbox 2.208 x 2.415 x 2e-07 mm, 0 faces, 0 solids (baked)
FEATURE [Part::Feature] path52377_0_5_0_4_2_4_4_8_9_2_0_5_5
  Placement = pos=(-191.198,-94.3836,0) rot=(0,0,1;0rad)
  shape: bbox 1.877 x 2.052 x 2e-07 mm, 0 faces, 0 solids (baked)
FEATURE [Part::Feature] path52456_0_5_5_7_7_7_1_7_0_0_6_4
  Placement = pos=(-196.698,-94.3836,0) rot=(0,0,1;0rad)
  shape: bbox 3.787 x 4.141 x 2e-07 mm, 0 faces, 0 solids (baked)
FEATURE [Part::Feature] path37937_8_6
  shape: bbox 1.702 x 2 x 2e-07 mm, 0 faces, 0 solids (baked)
FEATURE [Part::Feature] path37931_6_7
  shape: bbox 1.7 x 2 x 2e-07 mm, 0 faces, 0 solids (baked)
FEATURE [Part::Feature] path37321_9_5
  shape: bbox 2.002 x 1.603 x 2e-07 mm, 0 faces, 0 solids (baked)
FEATURE [Part::Feature] path37327_3_6
  shape: bbox 2.002 x 1.601 x 2e-07 mm, 0 faces, 0 solids (baked)
FEATURE [Part::Feature] path37329_6_1
  shape: bbox 2.002 x 1.603 x 2e-07 mm, 0 faces, 0 solids (baked)
FEATURE [Part::Feature] path37333_00_0
  shape: bbox 2.002 x 1.603 x 2e-07 mm, 0 faces, 0 solids (baked)
FEATURE [Part::Feature] circle37301_1_8
  Placement = pos=(227.782,-141.699,0) rot=(0,0,1;0rad)
  shape: bbox 0.8832 x 0.9658 x 2e-07 mm, 0 faces, 0 solids (baked)
FEATURE [Part::Feature] circle37295_7_4
  Placement = pos=(234.782,-141.699,0) rot=(0,0,1;0rad)
  shape: bbox 0.8832 x 0.9658 x 2e-07 mm, 0 faces, 0 solids (baked)
FEATURE [Part::Feature] rect117948_11_2
  shape: bbox 1.7 x 49.96 x 2e-07 mm, 0 faces, 0 solids (baked)
FEATURE [Part::Feature] rect117948_2_00_4
  shape: bbox 1.7 x 49.96 x 2e-07 mm, 0 faces, 0 solids (baked)
FEATURE [Part::Feature] path61609_4_5_7_9_4_80_0_4
  shape: bbox 15 x 7.701 x 2e-07 mm, 0 faces, 0 solids (baked)
FEATURE [Part::Feature] path61609_4_5_7_9_4_80_0_3_84
  shape: bbox 15 x 7.701 x 2e-07 mm, 0 faces, 0 solids (baked)
FEATURE [Part::Feature] path61609_4_5_7_9_4_80_0_8_5
  shape: bbox 15 x 7.701 x 2e-07 mm, 0 faces, 0 solids (baked)
FEATURE [Part::Feature] path61609_4_5_7_9_4_80_0_3_8_08
  shape: bbox 15 x 7.701 x 2e-07 mm, 0 faces, 0 solids (baked)
FEATURE [Part::Feature] path61609_4_5_7_9_4_80_0_3_8_6_37
  shape: bbox 15 x 7.701 x 2e-07 mm, 0 faces, 0 solids (baked)
FEATURE [Part::Feature] path61609_4_5_7_9_4_80_0_8_3_4
  shape: bbox 15 x 7.701 x 2e-07 mm, 0 faces, 0 solids (baked)
FEATURE [Part::Feature] path61609_4_5_7_9_4_80_0_3_8_9_8
  shape: bbox 15 x 7.701 x 2e-07 mm, 0 faces, 0 solids (baked)
FEATURE [Part::Feature] path61609_4_5_7_9_4_80_0_3_8_6_1_7
  shape: bbox 15 x 7.701 x 2e-07 mm, 0 faces, 0 solids (baked)
FEATURE [Part::Feature] path61609_4_5_7_9_4_80_0_8_7_4
  shape: bbox 15 x 7.701 x 2e-07 mm, 0 faces, 0 solids (baked)
FEATURE [Part::Feature] path61609_4_5_7_9_4_80_0_3_8_91_7
  shape: bbox 15 x 7.701 x 2e-07 mm, 0 faces, 0 solids (baked)
FEATURE [Part::Feature] path61609_4_5_7_9_4_80_0_3_8_6_3_5
  shape: bbox 15 x 7.701 x 2e-07 mm, 0 faces, 0 solids (baked)
FEATURE [Part::Feature] path61609_4_5_7_9_4_80_0_8_8_0
  shape: bbox 15 x 7.701 x 2e-07 mm, 0 faces, 0 solids (baked)
FEATURE [Part::Feature] path61609_4_5_7_9_4_80_0_3_8_0_5
  shape: bbox 15 x 7.701 x 2e-07 mm, 0 faces, 0 solids (baked)
FEATURE [Part::Feature] path61609_4_5_7_9_4_80_0_3_8_6_7_1
  shape: bbox 15 x 7.701 x 2e-07 mm, 0 faces, 0 solids (baked)
FEATURE [Part::Feature] path61609_4_5_7_9_4_80_0_8_2_8
  shape: bbox 15 x 7.701 x 2e-07 mm, 0 faces, 0 solids (baked)
FEATURE [Part::Feature] path61609_4_5_7_9_4_80_0_3_8_60_1
  shape: bbox 15 x 7.701 x 2e-07 mm, 0 faces, 0 solids (baked)
FEATURE [Part::Feature] path61609_4_5_7_9_4_80_0_3_8_6_4_3
  shape: bbox 15 x 7.701 x 2e-07 mm, 0 faces, 0 solids (baked)
FEATURE [Part::Feature] path52377_09_3_5_7_6_7_3
  Placement = pos=(-143.035,-172.587,0) rot=(0,0,1;0rad)
  shape: bbox 2.028 x 2.027 x 2e-07 mm, 0 faces, 0 solids (baked)
FEATURE [Part::Feature] path52401_71_2_5_9_2_77_3
  Placement = pos=(-142.535,-176.387,0) rot=(0,0,1;0rad)
  shape: bbox 2.386 x 2.384 x 2e-07 mm, 0 faces, 0 solids (baked)
FEATURE [Part::Feature] path52401_7_8_1_1_7_3_9_0
  Placement = pos=(-137.535,-178.487,0) rot=(0,0,1;0rad)
  shape: bbox 2.386 x 2.384 x 2e-07 mm, 0 faces, 0 solids (baked)
FEATURE [Part::Feature] path52377_0_5_0_1_9_1_5_5
  Placement = pos=(-132.035,-172.587,0) rot=(0,0,1;0rad)
  shape: bbox 2.028 x 2.027 x 2e-07 mm, 0 faces, 0 solids (baked)
FEATURE [Part::Feature] path52456_0_5_2_2_2_3_5
  Placement = pos=(-137.535,-172.587,0) rot=(0,0,1;0rad)
  shape: bbox 4.091 x 4.089 x 2e-07 mm, 0 faces, 0 solids (baked)
FEATURE [Part::Feature] path52377_09_3_5_7_6_0_0_2
  Placement = pos=(-279.563,-2.13117,0) rot=(0,0,1;0rad)
  shape: bbox 2.046 x 1.999 x 2e-07 mm, 0 faces, 0 solids (baked)
FEATURE [Part::Feature] path52401_71_2_5_9_2_7_5_4
  Placement = pos=(-279.063,-5.93117,0) rot=(0,0,1;0rad)
  shape: bbox 2.407 x 2.351 x 2e-07 mm, 0 faces, 0 solids (baked)
FEATURE [Part::Feature] path52401_7_8_1_1_7_3_8_4_4
  Placement = pos=(-274.063,-8.03117,0) rot=(0,0,1;0rad)
  shape: bbox 2.407 x 2.351 x 2e-07 mm, 0 faces, 0 solids (baked)
FEATURE [Part::Feature] path52377_0_5_0_1_9_1_0_6_9
  Placement = pos=(-268.563,-2.13117,0) rot=(0,0,1;0rad)
  shape: bbox 2.046 x 1.999 x 2e-07 mm, 0 faces, 0 solids (baked)
FEATURE [Part::Feature] path52456_0_5_2_2_2_9_9_3
  Placement = pos=(-274.063,-2.13117,0) rot=(0,0,1;0rad)
  shape: bbox 4.128 x 4.033 x 2e-07 mm, 0 faces, 0 solids (baked)
FEATURE [Part::Feature] path52377_09_3_5_7_6_6_7_9
  Placement = pos=(-249.546,-70.6289,0) rot=(0,0,1;0rad)
  shape: bbox 2.026 x 2.027 x 2e-07 mm, 0 faces, 0 solids (baked)
FEATURE [Part::Feature] path52401_71_2_5_9_2_1_4_5
  Placement = pos=(-249.046,-74.4289,0) rot=(0,0,1;0rad)
  shape: bbox 2.384 x 2.385 x 2e-07 mm, 0 faces, 0 solids (baked)
FEATURE [Part::Feature] path52401_7_8_1_1_7_3_1_9_1
  Placement = pos=(-244.046,-76.5289,0) rot=(0,0,1;0rad)
  shape: bbox 2.384 x 2.385 x 2e-07 mm, 0 faces, 0 solids (baked)
FEATURE [Part::Feature] path52377_0_5_0_1_9_1_3_9_3
  Placement = pos=(-238.546,-70.6289,0) rot=(0,0,1;0rad)
  shape: bbox 2.026 x 2.027 x 2e-07 mm, 0 faces, 0 solids (baked)
FEATURE [Part::Feature] path52456_0_5_2_2_2_5_8_5
  Placement = pos=(-244.046,-70.6289,0) rot=(0,0,1;0rad)
  shape: bbox 4.088 x 4.091 x 2e-07 mm, 0 faces, 0 solids (baked)
FEATURE [Part::Feature] path52377_09_3_5_7_6_4_7_2
  Placement = pos=(-202.897,-128.725,0) rot=(0,0,1;0rad)
  shape: bbox 1.997 x 2.046 x 2e-07 mm, 0 faces, 0 solids (baked)
FEATURE [Part::Feature] path52401_71_2_5_9_2_8_0_6
  Placement = pos=(-202.397,-132.525,0) rot=(0,0,1;0rad)
  shape: bbox 2.349 x 2.407 x 2e-07 mm, 0 faces, 0 solids (baked)
FEATURE [Part::Feature] path52401_7_8_1_1_7_3_6_7_6
  Placement = pos=(-197.397,-134.625,0) rot=(0,0,1;0rad)
  shape: bbox 2.349 x 2.407 x 2e-07 mm, 0 faces, 0 solids (baked)
FEATURE [Part::Feature] path52377_0_5_0_1_9_1_4_7_5
  Placement = pos=(-191.897,-128.725,0) rot=(0,0,1;0rad)
  shape: bbox 1.997 x 2.046 x 2e-07 mm, 0 faces, 0 solids (baked)
FEATURE [Part::Feature] path52456_0_5_2_2_2_7_4_6
  Placement = pos=(-197.397,-128.725,0) rot=(0,0,1;0rad)
  shape: bbox 4.029 x 4.128 x 2e-07 mm, 0 faces, 0 solids (baked)
FEATURE [Part::Feature] path61609_4_5_7_9_4_80_0_8_2_8_3
  shape: bbox 15.57 x 9.662 x 2e-07 mm, 0 faces, 0 solids (baked)
FEATURE [Part::Feature] path61609_4_5_7_9_4_80_0_8_2_8_3_6
  shape: bbox 16.06 x 7.248 x 2e-07 mm, 0 faces, 0 solids (baked)
FEATURE [Part::Feature] path61609_4_5_7_9_4_80_0_8_2_8_3_69
  shape: bbox 15.46 x 7.643 x 2e-07 mm, 0 faces, 0 solids (baked)
FEATURE [Part::Feature] path61609_4_5_7_9_4_80_0_8_2_8_3_7
  shape: bbox 14.99 x 9.16 x 2e-07 mm, 0 faces, 0 solids (baked)
FEATURE [Part::Extrusion] Extrude160
  Base = -> path52377_09_3_1_8_87_9
  Dir = (0,0,1)
  DirMode = 0
  FaceMakerClass = Part::FaceMakerBullseye
  LengthFwd = 2
  LengthRev = 0
  Solid = true
  Symmetric = false
FEATURE [Part::Extrusion] Extrude161
  Base = -> path52401_71_2_4_9_8_2
  Dir = (0,0,1)
  DirMode = 0
  FaceMakerClass = Part::FaceMakerBullseye
  LengthFwd = 2
  LengthRev = 0
  Solid = true
  Symmetric = false
FEATURE [Part::Extrusion] Extrude162
  Base = -> path52401_7_8_1_8_2_30_6
  Dir = (0,0,1)
  DirMode = 0
  FaceMakerClass = Part::FaceMakerBullseye
  LengthFwd = 2
  LengthRev = 0
  Solid = true
  Symmetric = false
FEATURE [Part::Extrusion] Extrude163
  Base = -> path52377_0_5_0_4_2_3_6
  Dir = (0,0,1)
  DirMode = 0
  FaceMakerClass = Part::FaceMakerBullseye
  LengthFwd = 2
  LengthRev = 0
  Solid = true
  Symmetric = false
FEATURE [Part::Extrusion] Extrude164
  Base = -> path52456_0_5_5_7_86_8
  Dir = (0,0,1)
  DirMode = 0
  FaceMakerClass = Part::FaceMakerBullseye
  LengthFwd = 2
  LengthRev = 0
  Solid = true
  Symmetric = false
FEATURE [Part::Extrusion] Extrude165
  Base = -> path52377_09_3_1_8_8_2_0
  Dir = (0,0,1)
  DirMode = 0
  FaceMakerClass = Part::FaceMakerBullseye
  LengthFwd = 2
  LengthRev = 0
  Solid = true
  Symmetric = false
FEATURE [Part::Extrusion] Extrude166
  Base = -> path52401_71_2_4_9_4_5_7
  Dir = (0,0,1)
  DirMode = 0
  FaceMakerClass = Part::FaceMakerBullseye
  LengthFwd = 2
  LengthRev = 0
  Solid = true
  Symmetric = false
FEATURE [Part::Extrusion] Extrude167
  Base = -> path52401_7_8_1_8_2_3_11_7
  Dir = (0,0,1)
  DirMode = 0
  FaceMakerClass = Part::FaceMakerBullseye
  LengthFwd = 2
  LengthRev = 0
  Solid = true
  Symmetric = false
FEATURE [Part::Extrusion] Extrude168
  Base = -> path52377_0_5_0_4_2_4_5_9
  Dir = (0,0,1)
  DirMode = 0
  FaceMakerClass = Part::FaceMakerBullseye
  LengthFwd = 2
  LengthRev = 0
  Solid = true
  Symmetric = false
FEATURE [Part::Extrusion] Extrude169
  Base = -> path52456_0_5_5_7_7_0_9
  Dir = (0,0,1)
  DirMode = 0
  FaceMakerClass = Part::FaceMakerBullseye
  LengthFwd = 2
  LengthRev = 0
  Solid = true
  Symmetric = false
FEATURE [Part::Extrusion] Extrude170
  Base = -> path52377_09_3_1_8_2_3_2
  Dir = (0,0,1)
  DirMode = 0
  FaceMakerClass = Part::FaceMakerBullseye
  LengthFwd = 2
  LengthRev = 0
  Solid = true
  Symmetric = false
FEATURE [Part::Extrusion] Extrude171
  Base = -> path52401_71_2_4_9_2_39_0
  Dir = (0,0,1)
  DirMode = 0
  FaceMakerClass = Part::FaceMakerBullseye
  LengthFwd = 2
  LengthRev = 0
  Solid = true
  Symmetric = false
FEATURE [Part::Extrusion] Extrude172
  Base = -> path52401_7_8_1_8_2_31_2_2
  Dir = (0,0,1)
  DirMode = 0
  FaceMakerClass = Part::FaceMakerBullseye
  LengthFwd = 2
  LengthRev = 0
  Solid = true
  Symmetric = false
FEATURE [Part::Extrusion] Extrude173
  Base = -> path52377_0_5_0_4_2_41_1_6
  Dir = (0,0,1)
  DirMode = 0
  FaceMakerClass = Part::FaceMakerBullseye
  LengthFwd = 2
  LengthRev = 0
  Solid = true
  Symmetric = false
FEATURE [Part::Extrusion] Extrude174
  Base = -> path52456_0_5_5_7_4_2_7
  Dir = (0,0,1)
  DirMode = 0
  FaceMakerClass = Part::FaceMakerBullseye
  LengthFwd = 2
  LengthRev = 0
  Solid = true
  Symmetric = false
FEATURE [Part::Extrusion] Extrude175
  Base = -> path52377_09_3_1_8_2_4_7_4
  Dir = (0,0,1)
  DirMode = 0
  FaceMakerClass = Part::FaceMakerBullseye
  LengthFwd = 2
  LengthRev = 0
  Solid = true
  Symmetric = false
FEATURE [Part::Extrusion] Extrude176
  Base = -> path52401_71_2_4_9_2_9_8_3
  Dir = (0,0,1)
  DirMode = 0
  FaceMakerClass = Part::FaceMakerBullseye
  LengthFwd = 2
  LengthRev = 0
  Solid = true
  Symmetric = false
FEATURE [Part::Extrusion] Extrude177
  Base = -> path52401_7_8_1_8_2_31_5_4_3
  Dir = (0,0,1)
  DirMode = 0
  FaceMakerClass = Part::FaceMakerBullseye
  LengthFwd = 2
  LengthRev = 0
  Solid = true
  Symmetric = false
FEATURE [Part::Extrusion] Extrude178
  Base = -> path52377_0_5_0_4_2_41_0_0_8
  Dir = (0,0,1)
  DirMode = 0
  FaceMakerClass = Part::FaceMakerBullseye
  LengthFwd = 2
  LengthRev = 0
  Solid = true
  Symmetric = false
FEATURE [Part::Extrusion] Extrude179
  Base = -> path52456_0_5_5_7_4_4_1_2
  Dir = (0,0,1)
  DirMode = 0
  FaceMakerClass = Part::FaceMakerBullseye
  LengthFwd = 2
  LengthRev = 0
  Solid = true
  Symmetric = false
FEATURE [Part::Extrusion] Extrude180
  Base = -> path52377_09_3_1_8_8_0_3_5
  Dir = (0,0,1)
  DirMode = 0
  FaceMakerClass = Part::FaceMakerBullseye
  LengthFwd = 2
  LengthRev = 0
  Solid = true
  Symmetric = false
FEATURE [Part::Extrusion] Extrude181
  Base = -> path52401_71_2_4_9_4_2_0_8
  Dir = (0,0,1)
  DirMode = 0
  FaceMakerClass = Part::FaceMakerBullseye
  LengthFwd = 2
  LengthRev = 0
  Solid = true
  Symmetric = false
FEATURE [Part::Extrusion] Extrude182
  Base = -> path52401_7_8_1_8_2_3_5_0_1
  Dir = (0,0,1)
  DirMode = 0
  FaceMakerClass = Part::FaceMakerBullseye
  LengthFwd = 2
  LengthRev = 0
  Solid = true
  Symmetric = false
FEATURE [Part::Extrusion] Extrude183
  Base = -> path52377_0_5_0_4_2_4_4_3_3
  Dir = (0,0,1)
  DirMode = 0
  FaceMakerClass = Part::FaceMakerBullseye
  LengthFwd = 2
  LengthRev = 0
  Solid = true
  Symmetric = false
FEATURE [Part::Extrusion] Extrude184
  Base = -> path52456_0_5_5_7_7_7_7_4
  Dir = (0,0,1)
  DirMode = 0
  FaceMakerClass = Part::FaceMakerBullseye
  LengthFwd = 2
  LengthRev = 0
  Solid = true
  Symmetric = false
FEATURE [Part::Extrusion] Extrude185
  Base = -> path52377_09_3_1_8_2_9_7_8
  Dir = (0,0,1)
  DirMode = 0
  FaceMakerClass = Part::FaceMakerBullseye
  LengthFwd = 2
  LengthRev = 0
  Solid = true
  Symmetric = false
FEATURE [Part::Extrusion] Extrude186
  Base = -> path52401_71_2_4_9_2_6_0_6
  Dir = (0,0,1)
  DirMode = 0
  FaceMakerClass = Part::FaceMakerBullseye
  LengthFwd = 2
  LengthRev = 0
  Solid = true
  Symmetric = false
FEATURE [Part::Extrusion] Extrude187
  Base = -> path52401_7_8_1_8_2_31_56_74_0
  Dir = (0,0,1)
  DirMode = 0
  FaceMakerClass = Part::FaceMakerBullseye
  LengthFwd = 2
  LengthRev = 0
  Solid = true
  Symmetric = false
FEATURE [Part::Extrusion] Extrude188
  Base = -> path52377_0_5_0_4_2_41_4_91_1
  Dir = (0,0,1)
  DirMode = 0
  FaceMakerClass = Part::FaceMakerBullseye
  LengthFwd = 2
  LengthRev = 0
  Solid = true
  Symmetric = false
FEATURE [Part::Extrusion] Extrude189
  Base = -> path52456_0_5_5_7_4_40_0_2
  Dir = (0,0,1)
  DirMode = 0
  FaceMakerClass = Part::FaceMakerBullseye
  LengthFwd = 2
  LengthRev = 0
  Solid = true
  Symmetric = false
FEATURE [Part::Extrusion] Extrude190
  Base = -> path52377_09_3_1_8_2_4_0_1_3
  Dir = (0,0,1)
  DirMode = 0
  FaceMakerClass = Part::FaceMakerBullseye
  LengthFwd = 2
  LengthRev = 0
  Solid = true
  Symmetric = false
FEATURE [Part::Extrusion] Extrude191
  Base = -> path52401_71_2_4_9_2_9_9_55_5
  Dir = (0,0,1)
  DirMode = 0
  FaceMakerClass = Part::FaceMakerBullseye
  LengthFwd = 2
  LengthRev = 0
  Solid = true
  Symmetric = false
FEATURE [Part::Extrusion] Extrude192
  Base = -> path52401_7_8_1_8_2_31_5_9_4_8
  Dir = (0,0,1)
  DirMode = 0
  FaceMakerClass = Part::FaceMakerBullseye
  LengthFwd = 2
  LengthRev = 0
  Solid = true
  Symmetric = false
FEATURE [Part::Extrusion] Extrude193
  Base = -> path52377_0_5_0_4_2_41_0_4_8_5
  Dir = (0,0,1)
  DirMode = 0
  FaceMakerClass = Part::FaceMakerBullseye
  LengthFwd = 2
  LengthRev = 0
  Solid = true
  Symmetric = false
FEATURE [Part::Extrusion] Extrude194
  Base = -> path52456_0_5_5_7_4_4_8_02_7
  Dir = (0,0,1)
  DirMode = 0
  FaceMakerClass = Part::FaceMakerBullseye
  LengthFwd = 2
  LengthRev = 0
  Solid = true
  Symmetric = false
FEATURE [Part::Extrusion] Extrude195
  Base = -> path52377_09_3_1_8_8_0_4_7_0
  Dir = (0,0,1)
  DirMode = 0
  FaceMakerClass = Part::FaceMakerBullseye
  LengthFwd = 2
  LengthRev = 0
  Solid = true
  Symmetric = false
FEATURE [Part::Extrusion] Extrude196
  Base = -> path52401_71_2_4_9_4_2_2_1_9
  Dir = (0,0,1)
  DirMode = 0
  FaceMakerClass = Part::FaceMakerBullseye
  LengthFwd = 2
  LengthRev = 0
  Solid = true
  Symmetric = false
FEATURE [Part::Extrusion] Extrude197
  Base = -> path52401_7_8_1_8_2_3_5_3_8_2
  Dir = (0,0,1)
  DirMode = 0
  FaceMakerClass = Part::FaceMakerBullseye
  LengthFwd = 2
  LengthRev = 0
  Solid = true
  Symmetric = false
FEATURE [Part::Extrusion] Extrude198
  Base = -> path52377_0_5_0_4_2_4_4_8_3_2
  Dir = (0,0,1)
  DirMode = 0
  FaceMakerClass = Part::FaceMakerBullseye
  LengthFwd = 2
  LengthRev = 0
  Solid = true
  Symmetric = false
FEATURE [Part::Extrusion] Extrude199
  Base = -> path52456_0_5_5_7_7_7_1_3_6
  Dir = (0,0,1)
  DirMode = 0
  FaceMakerClass = Part::FaceMakerBullseye
  LengthFwd = 2
  LengthRev = 0
  Solid = true
  Symmetric = false
FEATURE [Part::Extrusion] Extrude200
  Base = -> path52377_09_3_1_8_2_9_5_3_6
  Dir = (0,0,1)
  DirMode = 0
  FaceMakerClass = Part::FaceMakerBullseye
  LengthFwd = 2
  LengthRev = 0
  Solid = true
  Symmetric = false
FEATURE [Part::Extrusion] Extrude201
  Base = -> path52401_71_2_4_9_2_6_3_64_9
  Dir = (0,0,1)
  DirMode = 0
  FaceMakerClass = Part::FaceMakerBullseye
  LengthFwd = 2
  LengthRev = 0
  Solid = true
  Symmetric = false
FEATURE [Part::Extrusion] Extrude202
  Base = -> path52401_7_8_1_8_2_31_56_1_9_8
  Dir = (0,0,1)
  DirMode = 0
  FaceMakerClass = Part::FaceMakerBullseye
  LengthFwd = 2
  LengthRev = 0
  Solid = true
  Symmetric = false
FEATURE [Part::Extrusion] Extrude203
  Base = -> path52377_0_5_0_4_2_41_4_8_1_3
  Dir = (0,0,1)
  DirMode = 0
  FaceMakerClass = Part::FaceMakerBullseye
  LengthFwd = 2
  LengthRev = 0
  Solid = true
  Symmetric = false
FEATURE [Part::Extrusion] Extrude204
  Base = -> path52456_0_5_5_7_4_40_5_0_6
  Dir = (0,0,1)
  DirMode = 0
  FaceMakerClass = Part::FaceMakerBullseye
  LengthFwd = 2
  LengthRev = 0
  Solid = true
  Symmetric = false
FEATURE [Part::Extrusion] Extrude205
  Base = -> path52377_09_3_1_8_2_4_0_5_8_4
  Dir = (0,0,1)
  DirMode = 0
  FaceMakerClass = Part::FaceMakerBullseye
  LengthFwd = 2
  LengthRev = 0
  Solid = true
  Symmetric = false
FEATURE [Part::Extrusion] Extrude206
  Base = -> path52401_71_2_4_9_2_9_9_5_64_7
  Dir = (0,0,1)
  DirMode = 0
  FaceMakerClass = Part::FaceMakerBullseye
  LengthFwd = 2
  LengthRev = 0
  Solid = true
  Symmetric = false
FEATURE [Part::Extrusion] Extrude207
  Base = -> path52401_7_8_1_8_2_31_5_9_9_9_3
  Dir = (0,0,1)
  DirMode = 0
  FaceMakerClass = Part::FaceMakerBullseye
  LengthFwd = 2
  LengthRev = 0
  Solid = true
  Symmetric = false
FEATURE [Part::Extrusion] Extrude208
  Base = -> path52377_0_5_0_4_2_41_0_4_1_4_0
  Dir = (0,0,1)
  DirMode = 0
  FaceMakerClass = Part::FaceMakerBullseye
  LengthFwd = 2
  LengthRev = 0
  Solid = true
  Symmetric = false
FEATURE [Part::Extrusion] Extrude209
  Base = -> path52456_0_5_5_7_4_4_8_5_4_4
  Dir = (0,0,1)
  DirMode = 0
  FaceMakerClass = Part::FaceMakerBullseye
  LengthFwd = 2
  LengthRev = 0
  Solid = true
  Symmetric = false
FEATURE [Part::Extrusion] Extrude210
  Base = -> path52377_09_3_1_8_8_0_4_5_6_9
  Dir = (0,0,1)
  DirMode = 0
  FaceMakerClass = Part::FaceMakerBullseye
  LengthFwd = 2
  LengthRev = 0
  Solid = true
  Symmetric = false
FEATURE [Part::Extrusion] Extrude211
  Base = -> path52401_71_2_4_9_4_2_2_8_5_1
  Dir = (0,0,1)
  DirMode = 0
  FaceMakerClass = Part::FaceMakerBullseye
  LengthFwd = 2
  LengthRev = 0
  Solid = true
  Symmetric = false
FEATURE [Part::Extrusion] Extrude212
  Base = -> path52401_7_8_1_8_2_3_5_3_4_2_3
  Dir = (0,0,1)
  DirMode = 0
  FaceMakerClass = Part::FaceMakerBullseye
  LengthFwd = 2
  LengthRev = 0
  Solid = true
  Symmetric = false
FEATURE [Part::Extrusion] Extrude213
  Base = -> path52377_0_5_0_4_2_4_4_8_9_1_6
  Dir = (0,0,1)
  DirMode = 0
  FaceMakerClass = Part::FaceMakerBullseye
  LengthFwd = 2
  LengthRev = 0
  Solid = true
  Symmetric = false
FEATURE [Part::Extrusion] Extrude214
  Base = -> path52456_0_5_5_7_7_7_1_7_8_9
  Dir = (0,0,1)
  DirMode = 0
  FaceMakerClass = Part::FaceMakerBullseye
  LengthFwd = 2
  LengthRev = 0
  Solid = true
  Symmetric = false
FEATURE [Part::Extrusion] Extrude215
  Base = -> path52377_09_3_1_8_2_9_5_4_8_4
  Dir = (0,0,1)
  DirMode = 0
  FaceMakerClass = Part::FaceMakerBullseye
  LengthFwd = 2
  LengthRev = 0
  Solid = true
  Symmetric = false
FEATURE [Part::Extrusion] Extrude216
  Base = -> path52401_71_2_4_9_2_6_3_6_9_9
  Dir = (0,0,1)
  DirMode = 0
  FaceMakerClass = Part::FaceMakerBullseye
  LengthFwd = 2
  LengthRev = 0
  Solid = true
  Symmetric = false
FEATURE [Part::Extrusion] Extrude217
  Base = -> path52401_7_8_1_8_2_31_56_1_3_7_7
  Dir = (0,0,1)
  DirMode = 0
  FaceMakerClass = Part::FaceMakerBullseye
  LengthFwd = 2
  LengthRev = 0
  Solid = true
  Symmetric = false
FEATURE [Part::Extrusion] Extrude218
  Base = -> path52377_0_5_0_4_2_41_4_8_8_6_8
  Dir = (0,0,1)
  DirMode = 0
  FaceMakerClass = Part::FaceMakerBullseye
  LengthFwd = 2
  LengthRev = 0
  Solid = true
  Symmetric = false
FEATURE [Part::Extrusion] Extrude219
  Base = -> path52456_0_5_5_7_4_40_5_1_45_0
  Dir = (0,0,1)
  DirMode = 0
  FaceMakerClass = Part::FaceMakerBullseye
  LengthFwd = 2
  LengthRev = 0
  Solid = true
  Symmetric = false
FEATURE [Part::Extrusion] Extrude220
  Base = -> path52377_09_3_1_8_2_4_0_5_0_4_8
  Dir = (0,0,1)
  DirMode = 0
  FaceMakerClass = Part::FaceMakerBullseye
  LengthFwd = 2
  LengthRev = 0
  Solid = true
  Symmetric = false
FEATURE [Part::Extrusion] Extrude221
  Base = -> path52401_71_2_4_9_2_9_9_5_6_8_4
  Dir = (0,0,1)
  DirMode = 0
  FaceMakerClass = Part::FaceMakerBullseye
  LengthFwd = 2
  LengthRev = 0
  Solid = true
  Symmetric = false
FEATURE [Part::Extrusion] Extrude222
  Base = -> path52401_7_8_1_8_2_31_5_9_9_0_0_2
  Dir = (0,0,1)
  DirMode = 0
  FaceMakerClass = Part::FaceMakerBullseye
  LengthFwd = 2
  LengthRev = 0
  Solid = true
  Symmetric = false
FEATURE [Part::Extrusion] Extrude223
  Base = -> path52377_0_5_0_4_2_41_0_4_1_8_44_4
  Dir = (0,0,1)
  DirMode = 0
  FaceMakerClass = Part::FaceMakerBullseye
  LengthFwd = 2
  LengthRev = 0
  Solid = true
  Symmetric = false
FEATURE [Part::Extrusion] Extrude224
  Base = -> path52456_0_5_5_7_4_4_8_5_8_8_3
  Dir = (0,0,1)
  DirMode = 0
  FaceMakerClass = Part::FaceMakerBullseye
  LengthFwd = 2
  LengthRev = 0
  Solid = true
  Symmetric = false
FEATURE [Part::Extrusion] Extrude225
  Base = -> path52377_09_3_1_8_8_0_4_5_8_91_9
  Dir = (0,0,1)
  DirMode = 0
  FaceMakerClass = Part::FaceMakerBullseye
  LengthFwd = 2
  LengthRev = 0
  Solid = true
  Symmetric = false
FEATURE [Part::Extrusion] Extrude226
  Base = -> path52401_71_2_4_9_4_2_2_8_7_5_0
  Dir = (0,0,1)
  DirMode = 0
  FaceMakerClass = Part::FaceMakerBullseye
  LengthFwd = 2
  LengthRev = 0
  Solid = true
  Symmetric = false
FEATURE [Part::Extrusion] Extrude227
  Base = -> path52401_7_8_1_8_2_3_5_3_4_4_44_4
  Dir = (0,0,1)
  DirMode = 0
  FaceMakerClass = Part::FaceMakerBullseye
  LengthFwd = 2
  LengthRev = 0
  Solid = true
  Symmetric = false
FEATURE [Part::Extrusion] Extrude228
  Base = -> path52377_0_5_0_4_2_4_4_8_9_2_9_3
  Dir = (0,0,1)
  DirMode = 0
  FaceMakerClass = Part::FaceMakerBullseye
  LengthFwd = 2
  LengthRev = 0
  Solid = true
  Symmetric = false
FEATURE [Part::Extrusion] Extrude229
  Base = -> path52456_0_5_5_7_7_7_1_7_0_2_7
  Dir = (0,0,1)
  DirMode = 0
  FaceMakerClass = Part::FaceMakerBullseye
  LengthFwd = 2
  LengthRev = 0
  Solid = true
  Symmetric = false
FEATURE [Part::Extrusion] Extrude230
  Base = -> path52377_09_3_1_8_2_9_5_4_9_5_7
  Dir = (0,0,1)
  DirMode = 0
  FaceMakerClass = Part::FaceMakerBullseye
  LengthFwd = 2
  LengthRev = 0
  Solid = true
  Symmetric = false
FEATURE [Part::Extrusion] Extrude231
  Base = -> path52401_71_2_4_9_2_6_3_6_8_5_8
  Dir = (0,0,1)
  DirMode = 0
  FaceMakerClass = Part::FaceMakerBullseye
  LengthFwd = 2
  LengthRev = 0
  Solid = true
  Symmetric = false
FEATURE [Part::Extrusion] Extrude232
  Base = -> path52401_7_8_1_8_2_31_56_1_3_0_2_9
  Dir = (0,0,1)
  DirMode = 0
  FaceMakerClass = Part::FaceMakerBullseye
  LengthFwd = 2
  LengthRev = 0
  Solid = true
  Symmetric = false
FEATURE [Part::Extrusion] Extrude233
  Base = -> path52377_0_5_0_4_2_41_4_8_8_0_5_5
  Dir = (0,0,1)
  DirMode = 0
  FaceMakerClass = Part::FaceMakerBullseye
  LengthFwd = 2
  LengthRev = 0
  Solid = true
  Symmetric = false
FEATURE [Part::Extrusion] Extrude234
  Base = -> path52456_0_5_5_7_4_40_5_1_5_56_6
  Dir = (0,0,1)
  DirMode = 0
  FaceMakerClass = Part::FaceMakerBullseye
  LengthFwd = 2
  LengthRev = 0
  Solid = true
  Symmetric = false
FEATURE [Part::Extrusion] Extrude235
  Base = -> path52377_09_3_1_8_2_4_0_5_0_2_7_9
  Dir = (0,0,1)
  DirMode = 0
  FaceMakerClass = Part::FaceMakerBullseye
  LengthFwd = 2
  LengthRev = 0
  Solid = true
  Symmetric = false
FEATURE [Part::Extrusion] Extrude236
  Base = -> path52401_71_2_4_9_2_9_9_5_6_2_6_5
  Dir = (0,0,1)
  DirMode = 0
  FaceMakerClass = Part::FaceMakerBullseye
  LengthFwd = 2
  LengthRev = 0
  Solid = true
  Symmetric = false
FEATURE [Part::Extrusion] Extrude237
  Base = -> path52401_7_8_1_8_2_31_5_9_9_0_7_2_4
  Dir = (0,0,1)
  DirMode = 0
  FaceMakerClass = Part::FaceMakerBullseye
  LengthFwd = 2
  LengthRev = 0
  Solid = true
  Symmetric = false
FEATURE [Part::Extrusion] Extrude238
  Base = -> path52377_0_5_0_4_2_41_0_4_1_8_4_4_5
  Dir = (0,0,1)
  DirMode = 0
  FaceMakerClass = Part::FaceMakerBullseye
  LengthFwd = 2
  LengthRev = 0
  Solid = true
  Symmetric = false
FEATURE [Part::Extrusion] Extrude239
  Base = -> path52456_0_5_5_7_4_4_8_5_8_0_3_1
  Dir = (0,0,1)
  DirMode = 0
  FaceMakerClass = Part::FaceMakerBullseye
  LengthFwd = 2
  LengthRev = 0
  Solid = true
  Symmetric = false
FEATURE [Part::Extrusion] Extrude240
  Base = -> path52377_09_3_1_8_8_0_4_5_8_9_1_3
  Dir = (0,0,1)
  DirMode = 0
  FaceMakerClass = Part::FaceMakerBullseye
  LengthFwd = 2
  LengthRev = 0
  Solid = true
  Symmetric = false
FEATURE [Part::Extrusion] Extrude241
  Base = -> path52401_71_2_4_9_4_2_2_8_7_6_2_4
  Dir = (0,0,1)
  DirMode = 0
  FaceMakerClass = Part::FaceMakerBullseye
  LengthFwd = 2
  LengthRev = 0
  Solid = true
  Symmetric = false
FEATURE [Part::Extrusion] Extrude242
  Base = -> path52401_7_8_1_8_2_3_5_3_4_4_8_8_9
  Dir = (0,0,1)
  DirMode = 0
  FaceMakerClass = Part::FaceMakerBullseye
  LengthFwd = 2
  LengthRev = 0
  Solid = true
  Symmetric = false
FEATURE [Part::Extrusion] Extrude243
  Base = -> path52377_0_5_0_4_2_4_4_8_9_2_0_5_5
  Dir = (0,0,1)
  DirMode = 0
  FaceMakerClass = Part::FaceMakerBullseye
  LengthFwd = 2
  LengthRev = 0
  Solid = true
  Symmetric = false
FEATURE [Part::Extrusion] Extrude244
  Base = -> path52456_0_5_5_7_7_7_1_7_0_0_6_4
  Dir = (0,0,1)
  DirMode = 0
  FaceMakerClass = Part::FaceMakerBullseye
  LengthFwd = 2
  LengthRev = 0
  Solid = true
  Symmetric = false
FEATURE [Part::Extrusion] Extrude245
  Base = -> path37937_8_6
  Dir = (0,0,1)
  DirMode = 0
  FaceMakerClass = Part::FaceMakerBullseye
  LengthFwd = 2
  LengthRev = 0
  Solid = true
  Symmetric = false
FEATURE [Part::Extrusion] Extrude246
  Base = -> path37931_6_7
  Dir = (0,0,1)
  DirMode = 0
  FaceMakerClass = Part::FaceMakerBullseye
  LengthFwd = 2
  LengthRev = 0
  Solid = true
  Symmetric = false
FEATURE [Part::Extrusion] Extrude247
  Base = -> path37321_9_5
  Dir = (0,0,1)
  DirMode = 0
  FaceMakerClass = Part::FaceMakerBullseye
  LengthFwd = 2
  LengthRev = 0
  Solid = true
  Symmetric = false
FEATURE [Part::Extrusion] Extrude248
  Base = -> path37327_3_6
  Dir = (0,0,1)
  DirMode = 0
  FaceMakerClass = Part::FaceMakerBullseye
  LengthFwd = 2
  LengthRev = 0
  Solid = true
  Symmetric = false
FEATURE [Part::Extrusion] Extrude249
  Base = -> path37329_6_1
  Dir = (0,0,1)
  DirMode = 0
  FaceMakerClass = Part::FaceMakerBullseye
  LengthFwd = 2
  LengthRev = 0
  Solid = true
  Symmetric = false
FEATURE [Part::Extrusion] Extrude250
  Base = -> path37333_00_0
  Dir = (0,0,1)
  DirMode = 0
  FaceMakerClass = Part::FaceMakerBullseye
  LengthFwd = 2
  LengthRev = 0
  Solid = true
  Symmetric = false
FEATURE [Part::Extrusion] Extrude251
  Base = -> circle37301_1_8
  Dir = (0,0,1)
  DirMode = 0
  FaceMakerClass = Part::FaceMakerBullseye
  LengthFwd = 2
  LengthRev = 0
  Solid = true
  Symmetric = false
FEATURE [Part::Extrusion] Extrude252
  Base = -> circle37295_7_4
  Dir = (0,0,1)
  DirMode = 0
  FaceMakerClass = Part::FaceMakerBullseye
  LengthFwd = 2
  LengthRev = 0
  Solid = true
  Symmetric = false
FEATURE [Part::Extrusion] Extrude253
  Base = -> rect117948_11_2
  Dir = (0,0,1)
  DirMode = 0
  FaceMakerClass = Part::FaceMakerBullseye
  LengthFwd = 2
  LengthRev = 0
  Solid = true
  Symmetric = false
FEATURE [Part::Extrusion] Extrude254
  Base = -> rect117948_2_00_4
  Dir = (0,0,1)
  DirMode = 0
  FaceMakerClass = Part::FaceMakerBullseye
  LengthFwd = 2
  LengthRev = 0
  Solid = true
  Symmetric = false
FEATURE [Part::Extrusion] Extrude255
  Base = -> path61609_4_5_7_9_4_80_0_4
  Dir = (0,0,1)
  DirMode = 0
  FaceMakerClass = Part::FaceMakerBullseye
  LengthFwd = 2
  LengthRev = 0
  Solid = true
  Symmetric = false
FEATURE [Part::Extrusion] Extrude256
  Base = -> path61609_4_5_7_9_4_80_0_3_84
  Dir = (0,0,1)
  DirMode = 0
  FaceMakerClass = Part::FaceMakerBullseye
  LengthFwd = 2
  LengthRev = 0
  Solid = true
  Symmetric = false
FEATURE [Part::Extrusion] Extrude257
  Base = -> path61609_4_5_7_9_4_80_0_8_5
  Dir = (0,0,1)
  DirMode = 0
  FaceMakerClass = Part::FaceMakerBullseye
  LengthFwd = 2
  LengthRev = 0
  Solid = true
  Symmetric = false
FEATURE [Part::Extrusion] Extrude258
  Base = -> path61609_4_5_7_9_4_80_0_3_8_08
  Dir = (0,0,1)
  DirMode = 0
  FaceMakerClass = Part::FaceMakerBullseye
  LengthFwd = 2
  LengthRev = 0
  Solid = true
  Symmetric = false
FEATURE [Part::Extrusion] Extrude259
  Base = -> path61609_4_5_7_9_4_80_0_3_8_6_37
  Dir = (0,0,1)
  DirMode = 0
  FaceMakerClass = Part::FaceMakerBullseye
  LengthFwd = 2
  LengthRev = 0
  Solid = true
  Symmetric = false
FEATURE [Part::Extrusion] Extrude260
  Base = -> path61609_4_5_7_9_4_80_0_8_3_4
  Dir = (0,0,1)
  DirMode = 0
  FaceMakerClass = Part::FaceMakerBullseye
  LengthFwd = 2
  LengthRev = 0
  Solid = true
  Symmetric = false
FEATURE [Part::Extrusion] Extrude261
  Base = -> path61609_4_5_7_9_4_80_0_3_8_9_8
  Dir = (0,0,1)
  DirMode = 0
  FaceMakerClass = Part::FaceMakerBullseye
  LengthFwd = 2
  LengthRev = 0
  Solid = true
  Symmetric = false
FEATURE [Part::Extrusion] Extrude262
  Base = -> path61609_4_5_7_9_4_80_0_3_8_6_1_7
  Dir = (0,0,1)
  DirMode = 0
  FaceMakerClass = Part::FaceMakerBullseye
  LengthFwd = 2
  LengthRev = 0
  Solid = true
  Symmetric = false
FEATURE [Part::Extrusion] Extrude263
  Base = -> path61609_4_5_7_9_4_80_0_8_7_4
  Dir = (0,0,1)
  DirMode = 0
  FaceMakerClass = Part::FaceMakerBullseye
  LengthFwd = 2
  LengthRev = 0
  Solid = true
  Symmetric = false
FEATURE [Part::Extrusion] Extrude264
  Base = -> path61609_4_5_7_9_4_80_0_3_8_91_7
  Dir = (0,0,1)
  DirMode = 0
  FaceMakerClass = Part::FaceMakerBullseye
  LengthFwd = 2
  LengthRev = 0
  Solid = true
  Symmetric = false
FEATURE [Part::Extrusion] Extrude265
  Base = -> path61609_4_5_7_9_4_80_0_3_8_6_3_5
  Dir = (0,0,1)
  DirMode = 0
  FaceMakerClass = Part::FaceMakerBullseye
  LengthFwd = 2
  LengthRev = 0
  Solid = true
  Symmetric = false
FEATURE [Part::Extrusion] Extrude266
  Base = -> path61609_4_5_7_9_4_80_0_8_8_0
  Dir = (0,0,1)
  DirMode = 0
  FaceMakerClass = Part::FaceMakerBullseye
  LengthFwd = 2
  LengthRev = 0
  Solid = true
  Symmetric = false
FEATURE [Part::Extrusion] Extrude267
  Base = -> path61609_4_5_7_9_4_80_0_3_8_0_5
  Dir = (0,0,1)
  DirMode = 0
  FaceMakerClass = Part::FaceMakerBullseye
  LengthFwd = 2
  LengthRev = 0
  Solid = true
  Symmetric = false
FEATURE [Part::Extrusion] Extrude268
  Base = -> path61609_4_5_7_9_4_80_0_3_8_6_7_1
  Dir = (0,0,1)
  DirMode = 0
  FaceMakerClass = Part::FaceMakerBullseye
  LengthFwd = 2
  LengthRev = 0
  Solid = true
  Symmetric = false
FEATURE [Part::Extrusion] Extrude269
  Base = -> path61609_4_5_7_9_4_80_0_8_2_8
  Dir = (0,0,1)
  DirMode = 0
  FaceMakerClass = Part::FaceMakerBullseye
  LengthFwd = 2
  LengthRev = 0
  Solid = true
  Symmetric = false
FEATURE [Part::Extrusion] Extrude270
  Base = -> path61609_4_5_7_9_4_80_0_3_8_60_1
  Dir = (0,0,1)
  DirMode = 0
  FaceMakerClass = Part::FaceMakerBullseye
  LengthFwd = 2
  LengthRev = 0
  Solid = true
  Symmetric = false
FEATURE [Part::Extrusion] Extrude271
  Base = -> path61609_4_5_7_9_4_80_0_3_8_6_4_3
  Dir = (0,0,1)
  DirMode = 0
  FaceMakerClass = Part::FaceMakerBullseye
  LengthFwd = 2
  LengthRev = 0
  Solid = true
  Symmetric = false
FEATURE [Part::Extrusion] Extrude272
  Base = -> path52377_09_3_5_7_6_7_3
  Dir = (0,0,1)
  DirMode = 0
  FaceMakerClass = Part::FaceMakerBullseye
  LengthFwd = 2
  LengthRev = 0
  Solid = true
  Symmetric = false
FEATURE [Part::Extrusion] Extrude273
  Base = -> path52401_71_2_5_9_2_77_3
  Dir = (0,0,1)
  DirMode = 0
  FaceMakerClass = Part::FaceMakerBullseye
  LengthFwd = 2
  LengthRev = 0
  Solid = true
  Symmetric = false
FEATURE [Part::Extrusion] Extrude274
  Base = -> path52401_7_8_1_1_7_3_9_0
  Dir = (0,0,1)
  DirMode = 0
  FaceMakerClass = Part::FaceMakerBullseye
  LengthFwd = 2
  LengthRev = 0
  Solid = true
  Symmetric = false
FEATURE [Part::Extrusion] Extrude275
  Base = -> path52377_0_5_0_1_9_1_5_5
  Dir = (0,0,1)
  DirMode = 0
  FaceMakerClass = Part::FaceMakerBullseye
  LengthFwd = 2
  LengthRev = 0
  Solid = true
  Symmetric = false
FEATURE [Part::Extrusion] Extrude276
  Base = -> path52456_0_5_2_2_2_3_5
  Dir = (0,0,1)
  DirMode = 0
  FaceMakerClass = Part::FaceMakerBullseye
  LengthFwd = 2
  LengthRev = 0
  Solid = true
  Symmetric = false
FEATURE [Part::Extrusion] Extrude277
  Base = -> path52377_09_3_5_7_6_0_0_2
  Dir = (0,0,1)
  DirMode = 0
  FaceMakerClass = Part::FaceMakerBullseye
  LengthFwd = 2
  LengthRev = 0
  Solid = true
  Symmetric = false
FEATURE [Part::Extrusion] Extrude278
  Base = -> path52401_71_2_5_9_2_7_5_4
  Dir = (0,0,1)
  DirMode = 0
  FaceMakerClass = Part::FaceMakerBullseye
  LengthFwd = 2
  LengthRev = 0
  Solid = true
  Symmetric = false
FEATURE [Part::Extrusion] Extrude279
  Base = -> path52401_7_8_1_1_7_3_8_4_4
  Dir = (0,0,1)
  DirMode = 0
  FaceMakerClass = Part::FaceMakerBullseye
  LengthFwd = 2
  LengthRev = 0
  Solid = true
  Symmetric = false
FEATURE [Part::Extrusion] Extrude280
  Base = -> path52377_0_5_0_1_9_1_0_6_9
  Dir = (0,0,1)
  DirMode = 0
  FaceMakerClass = Part::FaceMakerBullseye
  LengthFwd = 2
  LengthRev = 0
  Solid = true
  Symmetric = false
FEATURE [Part::Extrusion] Extrude281
  Base = -> path52456_0_5_2_2_2_9_9_3
  Dir = (0,0,1)
  DirMode = 0
  FaceMakerClass = Part::FaceMakerBullseye
  LengthFwd = 2
  LengthRev = 0
  Solid = true
  Symmetric = false
FEATURE [Part::Extrusion] Extrude282
  Base = -> path52377_09_3_5_7_6_6_7_9
  Dir = (0,0,1)
  DirMode = 0
  FaceMakerClass = Part::FaceMakerBullseye
  LengthFwd = 2
  LengthRev = 0
  Solid = true
  Symmetric = false
FEATURE [Part::Extrusion] Extrude283
  Base = -> path52401_71_2_5_9_2_1_4_5
  Dir = (0,0,1)
  DirMode = 0
  FaceMakerClass = Part::FaceMakerBullseye
  LengthFwd = 2
  LengthRev = 0
  Solid = true
  Symmetric = false
FEATURE [Part::Extrusion] Extrude284
  Base = -> path52401_7_8_1_1_7_3_1_9_1
  Dir = (0,0,1)
  DirMode = 0
  FaceMakerClass = Part::FaceMakerBullseye
  LengthFwd = 2
  LengthRev = 0
  Solid = true
  Symmetric = false
FEATURE [Part::Extrusion] Extrude285
  Base = -> path52377_0_5_0_1_9_1_3_9_3
  Dir = (0,0,1)
  DirMode = 0
  FaceMakerClass = Part::FaceMakerBullseye
  LengthFwd = 2
  LengthRev = 0
  Solid = true
  Symmetric = false
FEATURE [Part::Extrusion] Extrude286
  Base = -> path52456_0_5_2_2_2_5_8_5
  Dir = (0,0,1)
  DirMode = 0
  FaceMakerClass = Part::FaceMakerBullseye
  LengthFwd = 2
  LengthRev = 0
  Solid = true
  Symmetric = false
FEATURE [Part::Extrusion] Extrude287
  Base = -> path52377_09_3_5_7_6_4_7_2
  Dir = (0,0,1)
  DirMode = 0
  FaceMakerClass = Part::FaceMakerBullseye
  LengthFwd = 2
  LengthRev = 0
  Solid = true
  Symmetric = false
FEATURE [Part::Extrusion] Extrude288
  Base = -> path52401_71_2_5_9_2_8_0_6
  Dir = (0,0,1)
  DirMode = 0
  FaceMakerClass = Part::FaceMakerBullseye
  LengthFwd = 2
  LengthRev = 0
  Solid = true
  Symmetric = false
FEATURE [Part::Extrusion] Extrude289
  Base = -> path52401_7_8_1_1_7_3_6_7_6
  Dir = (0,0,1)
  DirMode = 0
  FaceMakerClass = Part::FaceMakerBullseye
  LengthFwd = 2
  LengthRev = 0
  Solid = true
  Symmetric = false
FEATURE [Part::Extrusion] Extrude290
  Base = -> path52377_0_5_0_1_9_1_4_7_5
  Dir = (0,0,1)
  DirMode = 0
  FaceMakerClass = Part::FaceMakerBullseye
  LengthFwd = 2
  LengthRev = 0
  Solid = true
  Symmetric = false
FEATURE [Part::Extrusion] Extrude291
  Base = -> path52456_0_5_2_2_2_7_4_6
  Dir = (0,0,1)
  DirMode = 0
  FaceMakerClass = Part::FaceMakerBullseye
  LengthFwd = 2
  LengthRev = 0
  Solid = true
  Symmetric = false
FEATURE [Part::Extrusion] Extrude292
  Base = -> path61609_4_5_7_9_4_80_0_8_2_8_3
  Dir = (0,0,1)
  DirMode = 0
  FaceMakerClass = Part::FaceMakerBullseye
  LengthFwd = 2
  LengthRev = 0
  Solid = true
  Symmetric = false
FEATURE [Part::Extrusion] Extrude293
  Base = -> path61609_4_5_7_9_4_80_0_8_2_8_3_6
  Dir = (0,0,1)
  DirMode = 0
  FaceMakerClass = Part::FaceMakerBullseye
  LengthFwd = 2
  LengthRev = 0
  Solid = true
  Symmetric = false
FEATURE [Part::Extrusion] Extrude294
  Base = -> path61609_4_5_7_9_4_80_0_8_2_8_3_69
  Dir = (0,0,1)
  DirMode = 0
  FaceMakerClass = Part::FaceMakerBullseye
  LengthFwd = 2
  LengthRev = 0
  Solid = true
  Symmetric = false
FEATURE [Part::Extrusion] Extrude295
  Base = -> path61609_4_5_7_9_4_80_0_8_2_8_3_7
  Dir = (0,0,1)
  DirMode = 0
  FaceMakerClass = Part::FaceMakerBullseye
  LengthFwd = 2
  LengthRev = 0
  Solid = true
  Symmetric = false
FEATURE [Part::MultiFuse] Fusion003  label="wells_right"
  Placement = pos=(0,0,1) rot=(0,0,1;0rad)
  Shapes = -> [Extrude295,Extrude160,Extrude161,Extrude162,Extrude163,Extrude164,Extrude165,Extrude166,Extrude167,Extrude168,Extrude169,Extrude170,Extrude171,Extrude172,Extrude173,Extrude174,Extrude175,Extrude176,Extrude177,Extrude178,Extrude179,Extrude180,Extrude181,Extrude182,Extrude183,Extrude184,Extrude185,Extrude186,Extrude187,Extrude188,Extrude189,Extrude190,Extrude191,Extrude192,Extrude193,Extrude194,+100 more]
FEATURE [Part::FeaturePython] XOR  # WARN: FeaturePython — macro-defined, semantics opaque (R4)
  Objects = -> [Fusion001,Extrude001,Extrude]
  Tolerance = 0
FEATURE [Part::FeaturePython] XOR001  # WARN: FeaturePython — macro-defined, semantics opaque (R4)
  Objects = -> [Extrude148,Extrude149,Fusion003]
  Tolerance = 0
FEATURE [Part::Mirroring] Part__Mirroring  label="XOR001 (Mirror #1)"
  Base = (0,0,0)
  Normal = (1,0,0)
  Placement = pos=(140,90,0) rot=(0,0,1;0rad)
  Source = -> XOR001
FEATURE [Part::MultiFuse] Fusion
  Shapes = -> [Part__Mirroring,XOR]
